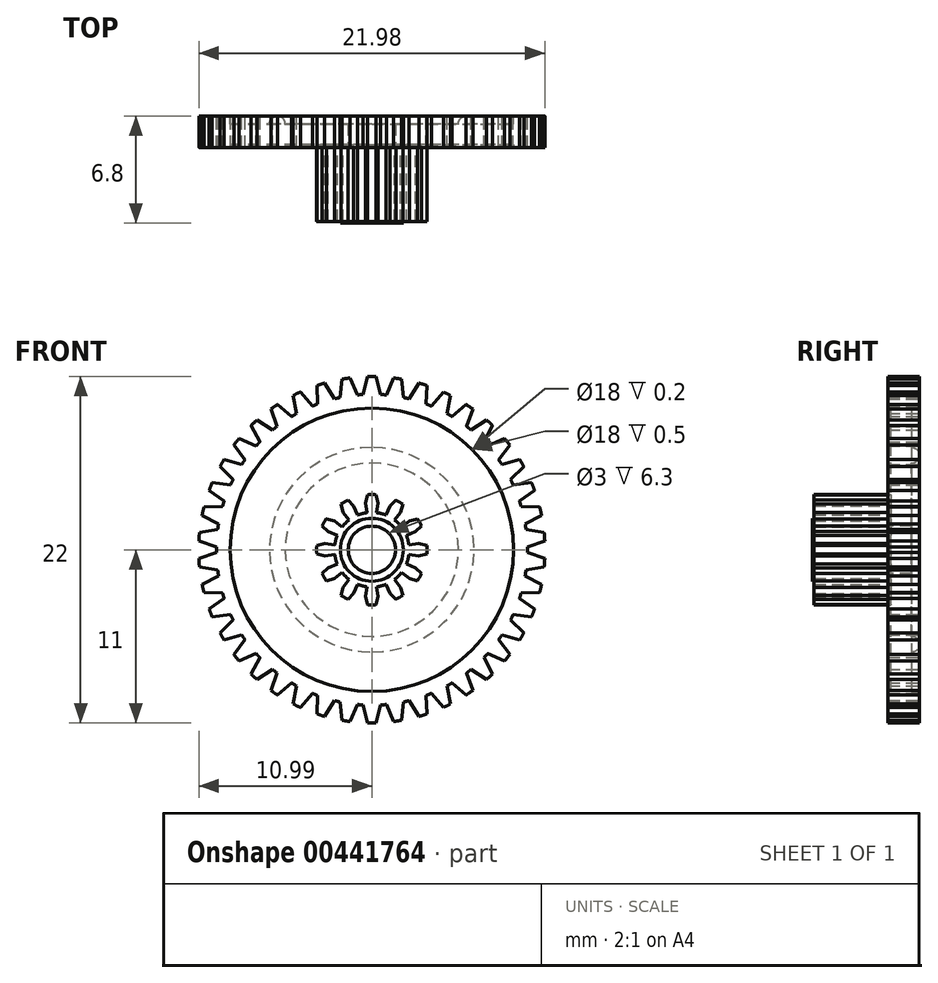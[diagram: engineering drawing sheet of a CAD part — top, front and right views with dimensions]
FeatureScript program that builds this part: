
annotation { "Feature Type Name" : "Feature", "Feature Type Description" : "" }
export const myFeature = defineFeature(function(context is Context, id is Id, definition is map)
    precondition{}
    {
        {
            var Q0;
            Q0=qCreatedBy(makeId("Front.planeOp"),FACE);
            var sketch = newSketch(context, id + "F0", { "sketchPlane" : qUnion([Q0])});
            skCircle(sketch, "E0", {"center": v(0, 0) * mm, "radius": 9.88 * mm});
            skSolve(sketch);
        }
        {
            var Q0;
            Q0 = qSketchRegion(id + "F0", true);
            extrude(context, id + "F1", {"entities" : qUnion([Q0]), "depth" : 2 * mm});
        }
        {
            var Q0;
            Q0=qCreatedBy(makeId("Front.planeOp"),FACE);
            var sketch = newSketch(context, id + "F2", { "sketchPlane" : qUnion([Q0])});
            skArc(sketch, "E1", {"start": v(0, 12) * mm, "mid": v(-0.22, 12) * mm, "end": v(-0.45, 12) * mm});
            skArc(sketch, "E2", {"start": v(0.26, 11) * mm, "mid": v(-0.08, 11) * mm, "end": v(-0.41, 11) * mm});
            skArc(sketch, "E3", {"start": v(0.4, 10.5) * mm, "mid": v(0, 10.5) * mm, "end": v(-0.4, 10.5) * mm});
            skCircle(sketch, "E4", {"center": v(0, 0) * mm, "radius": 9.88 * mm});
            skLineSegment(sketch, "E5", {"start": v(0, 0) * mm, "end": v(0, 15.41) * mm});
            skLineSegment(sketch, "E6", {"start": v(0, 0) * mm, "end": v(-0.5, 13.31) * mm});
            skLineSegment(sketch, "E7", {"start": v(-0.4, 10.5) * mm, "end": v(-0.56, 9.86) * mm});
            skLineSegment(sketch, "E8", {"start": v(0.4, 10.5) * mm, "end": v(0.56, 9.86) * mm});
            skLineSegment(sketch, "E9", {"start": v(-0.4, 10.5) * mm, "end": v(-0.26, 11) * mm});
            skLineSegment(sketch, "E10", {"start": v(-0.26, 11) * mm, "end": v(0, 12) * mm});
            skLineSegment(sketch, "E11", {"start": v(0, 12) * mm, "end": v(0.26, 11) * mm});
            skLineSegment(sketch, "E12", {"start": v(0.26, 11) * mm, "end": v(0.4, 10.5) * mm});
            skLineSegment(sketch, "E13.1.0", {"start": v(-1.95, 10.32) * mm, "end": v(-2.02, 9.67) * mm});
            skLineSegment(sketch, "E13.1.1", {"start": v(-1.95, 10.32) * mm, "end": v(-1.9, 10.84) * mm});
            skLineSegment(sketch, "E13.1.2", {"start": v(-1.38, 10.91) * mm, "end": v(-1.18, 10.43) * mm});
            skLineSegment(sketch, "E13.1.3", {"start": v(-1.18, 10.43) * mm, "end": v(-0.92, 9.83) * mm});
            skArc(sketch, "E13.1.4", {"start": v(-1.38, 10.91) * mm, "mid": v(-1.71, 10.87) * mm, "end": v(-2.05, 10.8) * mm});
            skLineSegment(sketch, "E13.2.0", {"start": v(-3.47, 9.91) * mm, "end": v(-3.44, 9.26) * mm});
            skLineSegment(sketch, "E13.2.1", {"start": v(-3.47, 9.91) * mm, "end": v(-3.5, 10.43) * mm});
            skLineSegment(sketch, "E13.2.2", {"start": v(-3, 10.59) * mm, "end": v(-2.72, 10.14) * mm});
            skLineSegment(sketch, "E13.2.3", {"start": v(-2.72, 10.14) * mm, "end": v(-2.37, 9.59) * mm});
            skArc(sketch, "E13.2.4", {"start": v(-3, 10.59) * mm, "mid": v(-3.31, 10.49) * mm, "end": v(-3.63, 10.38) * mm});
            skLineSegment(sketch, "E13.3.0", {"start": v(-4.9, 9.28) * mm, "end": v(-4.78, 8.64) * mm});
            skLineSegment(sketch, "E13.3.1", {"start": v(-4.9, 9.28) * mm, "end": v(-5, 9.8) * mm});
            skLineSegment(sketch, "E13.3.2", {"start": v(-4.54, 10.02) * mm, "end": v(-4.2, 9.62) * mm});
            skLineSegment(sketch, "E13.3.3", {"start": v(-4.2, 9.62) * mm, "end": v(-3.78, 9.12) * mm});
            skArc(sketch, "E13.3.4", {"start": v(-4.54, 10.02) * mm, "mid": v(-4.84, 9.88) * mm, "end": v(-5.14, 9.73) * mm});
            skLineSegment(sketch, "E13.4.0", {"start": v(-6.24, 8.45) * mm, "end": v(-6.01, 7.83) * mm});
            skLineSegment(sketch, "E13.4.1", {"start": v(-6.24, 8.45) * mm, "end": v(-6.41, 8.94) * mm});
            skLineSegment(sketch, "E13.4.2", {"start": v(-5.98, 9.23) * mm, "end": v(-5.59, 8.9) * mm});
            skLineSegment(sketch, "E13.4.3", {"start": v(-5.59, 8.9) * mm, "end": v(-5.1, 8.46) * mm});
            skArc(sketch, "E13.4.4", {"start": v(-5.98, 9.23) * mm, "mid": v(-6.26, 9.05) * mm, "end": v(-6.53, 8.85) * mm});
            skLineSegment(sketch, "E13.5.0", {"start": v(-7.42, 7.42) * mm, "end": v(-7.11, 6.85) * mm});
            skLineSegment(sketch, "E13.5.1", {"start": v(-7.42, 7.42) * mm, "end": v(-7.67, 7.88) * mm});
            skLineSegment(sketch, "E13.5.2", {"start": v(-7.29, 8.24) * mm, "end": v(-6.85, 7.96) * mm});
            skLineSegment(sketch, "E13.5.3", {"start": v(-6.85, 7.96) * mm, "end": v(-6.3, 7.6) * mm});
            skArc(sketch, "E13.5.4", {"start": v(-7.29, 8.24) * mm, "mid": v(-7.54, 8.01) * mm, "end": v(-7.78, 7.78) * mm});
            skLineSegment(sketch, "E13.6.0", {"start": v(-8.45, 6.24) * mm, "end": v(-8.06, 5.71) * mm});
            skLineSegment(sketch, "E13.6.1", {"start": v(-8.45, 6.24) * mm, "end": v(-8.76, 6.65) * mm});
            skLineSegment(sketch, "E13.6.2", {"start": v(-8.43, 7.06) * mm, "end": v(-7.96, 6.85) * mm});
            skLineSegment(sketch, "E13.6.3", {"start": v(-7.96, 6.85) * mm, "end": v(-7.36, 6.58) * mm});
            skArc(sketch, "E13.6.4", {"start": v(-8.43, 7.06) * mm, "mid": v(-8.65, 6.8) * mm, "end": v(-8.85, 6.53) * mm});
            skLineSegment(sketch, "E13.7.0", {"start": v(-9.28, 4.9) * mm, "end": v(-8.82, 4.45) * mm});
            skLineSegment(sketch, "E13.7.1", {"start": v(-9.28, 4.9) * mm, "end": v(-9.65, 5.27) * mm});
            skLineSegment(sketch, "E13.7.2", {"start": v(-9.4, 5.72) * mm, "end": v(-8.9, 5.59) * mm});
            skLineSegment(sketch, "E13.7.3", {"start": v(-8.9, 5.59) * mm, "end": v(-8.26, 5.41) * mm});
            skArc(sketch, "E13.7.4", {"start": v(-9.4, 5.72) * mm, "mid": v(-9.56, 5.43) * mm, "end": v(-9.73, 5.14) * mm});
            skLineSegment(sketch, "E13.8.0", {"start": v(-9.91, 3.47) * mm, "end": v(-9.38, 3.08) * mm});
            skLineSegment(sketch, "E13.8.1", {"start": v(-9.91, 3.47) * mm, "end": v(-10.33, 3.77) * mm});
            skLineSegment(sketch, "E13.8.2", {"start": v(-10.14, 4.26) * mm, "end": v(-9.62, 4.2) * mm});
            skLineSegment(sketch, "E13.8.3", {"start": v(-9.62, 4.2) * mm, "end": v(-8.97, 4.12) * mm});
            skArc(sketch, "E13.8.4", {"start": v(-10.14, 4.26) * mm, "mid": v(-10.27, 3.95) * mm, "end": v(-10.38, 3.63) * mm});
            skLineSegment(sketch, "E13.9.0", {"start": v(-10.32, 1.95) * mm, "end": v(-9.74, 1.65) * mm});
            skLineSegment(sketch, "E13.9.1", {"start": v(-10.32, 1.95) * mm, "end": v(-10.78, 2.2) * mm});
            skLineSegment(sketch, "E13.9.2", {"start": v(-10.66, 2.7) * mm, "end": v(-10.14, 2.72) * mm});
            skLineSegment(sketch, "E13.9.3", {"start": v(-10.14, 2.72) * mm, "end": v(-9.49, 2.74) * mm});
            skArc(sketch, "E13.9.4", {"start": v(-10.66, 2.7) * mm, "mid": v(-10.74, 2.37) * mm, "end": v(-10.8, 2.05) * mm});
            skLineSegment(sketch, "E13.10.0", {"start": v(-10.5, 0.4) * mm, "end": v(-9.87, 0.18) * mm});
            skLineSegment(sketch, "E13.10.1", {"start": v(-10.5, 0.4) * mm, "end": v(-10.99, 0.56) * mm});
            skLineSegment(sketch, "E13.10.2", {"start": v(-10.95, 1.08) * mm, "end": v(-10.43, 1.18) * mm});
            skLineSegment(sketch, "E13.10.3", {"start": v(-10.43, 1.18) * mm, "end": v(-9.8, 1.3) * mm});
            skArc(sketch, "E13.10.4", {"start": v(-10.95, 1.08) * mm, "mid": v(-10.97, 0.75) * mm, "end": v(-11, 0.41) * mm});
            skLineSegment(sketch, "E13.11.0", {"start": v(-10.43, -1.18) * mm, "end": v(-9.8, -1.3) * mm});
            skLineSegment(sketch, "E13.11.1", {"start": v(-10.43, -1.18) * mm, "end": v(-10.95, -1.08) * mm});
            skLineSegment(sketch, "E13.11.2", {"start": v(-10.99, -0.56) * mm, "end": v(-10.5, -0.4) * mm});
            skLineSegment(sketch, "E13.11.3", {"start": v(-10.5, -0.4) * mm, "end": v(-9.87, -0.18) * mm});
            skArc(sketch, "E13.11.4", {"start": v(-10.99, -0.56) * mm, "mid": v(-10.96, -0.9) * mm, "end": v(-10.93, -1.23) * mm});
            skLineSegment(sketch, "E13.12.0", {"start": v(-10.14, -2.72) * mm, "end": v(-9.49, -2.74) * mm});
            skLineSegment(sketch, "E13.12.1", {"start": v(-10.14, -2.72) * mm, "end": v(-10.66, -2.7) * mm});
            skLineSegment(sketch, "E13.12.2", {"start": v(-10.78, -2.2) * mm, "end": v(-10.32, -1.95) * mm});
            skLineSegment(sketch, "E13.12.3", {"start": v(-10.32, -1.95) * mm, "end": v(-9.74, -1.65) * mm});
            skArc(sketch, "E13.12.4", {"start": v(-10.78, -2.2) * mm, "mid": v(-10.7, -2.52) * mm, "end": v(-10.63, -2.85) * mm});
            skLineSegment(sketch, "E13.13.0", {"start": v(-9.62, -4.2) * mm, "end": v(-8.97, -4.12) * mm});
            skLineSegment(sketch, "E13.13.1", {"start": v(-9.62, -4.2) * mm, "end": v(-10.14, -4.26) * mm});
            skLineSegment(sketch, "E13.13.2", {"start": v(-10.33, -3.77) * mm, "end": v(-9.91, -3.47) * mm});
            skLineSegment(sketch, "E13.13.3", {"start": v(-9.91, -3.47) * mm, "end": v(-9.38, -3.08) * mm});
            skArc(sketch, "E13.13.4", {"start": v(-10.33, -3.77) * mm, "mid": v(-10.21, -4.09) * mm, "end": v(-10.08, -4.4) * mm});
            skLineSegment(sketch, "E13.14.0", {"start": v(-8.9, -5.59) * mm, "end": v(-8.26, -5.41) * mm});
            skLineSegment(sketch, "E13.14.1", {"start": v(-8.9, -5.59) * mm, "end": v(-9.4, -5.72) * mm});
            skLineSegment(sketch, "E13.14.2", {"start": v(-9.65, -5.27) * mm, "end": v(-9.28, -4.9) * mm});
            skLineSegment(sketch, "E13.14.3", {"start": v(-9.28, -4.9) * mm, "end": v(-8.82, -4.45) * mm});
            skArc(sketch, "E13.14.4", {"start": v(-9.65, -5.27) * mm, "mid": v(-9.49, -5.56) * mm, "end": v(-9.31, -5.85) * mm});
            skLineSegment(sketch, "E13.15.0", {"start": v(-7.96, -6.85) * mm, "end": v(-7.36, -6.58) * mm});
            skLineSegment(sketch, "E13.15.1", {"start": v(-7.96, -6.85) * mm, "end": v(-8.43, -7.06) * mm});
            skLineSegment(sketch, "E13.15.2", {"start": v(-8.76, -6.65) * mm, "end": v(-8.45, -6.24) * mm});
            skLineSegment(sketch, "E13.15.3", {"start": v(-8.45, -6.24) * mm, "end": v(-8.06, -5.71) * mm});
            skArc(sketch, "E13.15.4", {"start": v(-8.76, -6.65) * mm, "mid": v(-8.55, -6.92) * mm, "end": v(-8.34, -7.18) * mm});
            skLineSegment(sketch, "E13.16.0", {"start": v(-6.85, -7.96) * mm, "end": v(-6.3, -7.6) * mm});
            skLineSegment(sketch, "E13.16.1", {"start": v(-6.85, -7.96) * mm, "end": v(-7.29, -8.24) * mm});
            skLineSegment(sketch, "E13.16.2", {"start": v(-7.67, -7.88) * mm, "end": v(-7.42, -7.42) * mm});
            skLineSegment(sketch, "E13.16.3", {"start": v(-7.42, -7.42) * mm, "end": v(-7.11, -6.85) * mm});
            skArc(sketch, "E13.16.4", {"start": v(-7.67, -7.88) * mm, "mid": v(-7.43, -8.11) * mm, "end": v(-7.18, -8.34) * mm});
            skLineSegment(sketch, "E13.17.0", {"start": v(-5.59, -8.9) * mm, "end": v(-5.1, -8.46) * mm});
            skLineSegment(sketch, "E13.17.1", {"start": v(-5.59, -8.9) * mm, "end": v(-5.98, -9.23) * mm});
            skLineSegment(sketch, "E13.17.2", {"start": v(-6.41, -8.94) * mm, "end": v(-6.24, -8.45) * mm});
            skLineSegment(sketch, "E13.17.3", {"start": v(-6.24, -8.45) * mm, "end": v(-6.01, -7.83) * mm});
            skArc(sketch, "E13.17.4", {"start": v(-6.41, -8.94) * mm, "mid": v(-6.13, -9.13) * mm, "end": v(-5.85, -9.31) * mm});
            skLineSegment(sketch, "E13.18.0", {"start": v(-4.2, -9.62) * mm, "end": v(-3.78, -9.12) * mm});
            skLineSegment(sketch, "E13.18.1", {"start": v(-4.2, -9.62) * mm, "end": v(-4.54, -10.02) * mm});
            skLineSegment(sketch, "E13.18.2", {"start": v(-5, -9.8) * mm, "end": v(-4.9, -9.28) * mm});
            skLineSegment(sketch, "E13.18.3", {"start": v(-4.9, -9.28) * mm, "end": v(-4.78, -8.64) * mm});
            skArc(sketch, "E13.18.4", {"start": v(-5, -9.8) * mm, "mid": v(-4.7, -9.94) * mm, "end": v(-4.4, -10.08) * mm});
            skLineSegment(sketch, "E13.19.0", {"start": v(-2.72, -10.14) * mm, "end": v(-2.37, -9.59) * mm});
            skLineSegment(sketch, "E13.19.1", {"start": v(-2.72, -10.14) * mm, "end": v(-3, -10.59) * mm});
            skLineSegment(sketch, "E13.19.2", {"start": v(-3.5, -10.43) * mm, "end": v(-3.47, -9.91) * mm});
            skLineSegment(sketch, "E13.19.3", {"start": v(-3.47, -9.91) * mm, "end": v(-3.44, -9.26) * mm});
            skArc(sketch, "E13.19.4", {"start": v(-3.5, -10.43) * mm, "mid": v(-3.17, -10.53) * mm, "end": v(-2.85, -10.63) * mm});
            skLineSegment(sketch, "E13.20.0", {"start": v(-1.18, -10.43) * mm, "end": v(-0.92, -9.83) * mm});
            skLineSegment(sketch, "E13.20.1", {"start": v(-1.18, -10.43) * mm, "end": v(-1.38, -10.91) * mm});
            skLineSegment(sketch, "E13.20.2", {"start": v(-1.9, -10.84) * mm, "end": v(-1.95, -10.32) * mm});
            skLineSegment(sketch, "E13.20.3", {"start": v(-1.95, -10.32) * mm, "end": v(-2.02, -9.67) * mm});
            skArc(sketch, "E13.20.4", {"start": v(-1.9, -10.84) * mm, "mid": v(-1.57, -10.89) * mm, "end": v(-1.23, -10.93) * mm});
            skLineSegment(sketch, "E13.21.0", {"start": v(0.4, -10.5) * mm, "end": v(0.56, -9.86) * mm});
            skLineSegment(sketch, "E13.21.1", {"start": v(0.4, -10.5) * mm, "end": v(0.26, -11) * mm});
            skLineSegment(sketch, "E13.21.2", {"start": v(-0.26, -11) * mm, "end": v(-0.4, -10.5) * mm});
            skLineSegment(sketch, "E13.21.3", {"start": v(-0.4, -10.5) * mm, "end": v(-0.56, -9.86) * mm});
            skArc(sketch, "E13.21.4", {"start": v(-0.26, -11) * mm, "mid": v(0.08, -11) * mm, "end": v(0.41, -11) * mm});
            skLineSegment(sketch, "E13.22.0", {"start": v(1.95, -10.32) * mm, "end": v(2.02, -9.67) * mm});
            skLineSegment(sketch, "E13.22.1", {"start": v(1.95, -10.32) * mm, "end": v(1.9, -10.84) * mm});
            skLineSegment(sketch, "E13.22.2", {"start": v(1.38, -10.91) * mm, "end": v(1.18, -10.43) * mm});
            skLineSegment(sketch, "E13.22.3", {"start": v(1.18, -10.43) * mm, "end": v(0.92, -9.83) * mm});
            skArc(sketch, "E13.22.4", {"start": v(1.38, -10.91) * mm, "mid": v(1.71, -10.87) * mm, "end": v(2.05, -10.8) * mm});
            skLineSegment(sketch, "E13.23.0", {"start": v(3.47, -9.91) * mm, "end": v(3.44, -9.26) * mm});
            skLineSegment(sketch, "E13.23.1", {"start": v(3.47, -9.91) * mm, "end": v(3.5, -10.43) * mm});
            skLineSegment(sketch, "E13.23.2", {"start": v(3, -10.59) * mm, "end": v(2.72, -10.14) * mm});
            skLineSegment(sketch, "E13.23.3", {"start": v(2.72, -10.14) * mm, "end": v(2.37, -9.59) * mm});
            skArc(sketch, "E13.23.4", {"start": v(3, -10.59) * mm, "mid": v(3.31, -10.49) * mm, "end": v(3.63, -10.38) * mm});
            skLineSegment(sketch, "E13.24.0", {"start": v(4.9, -9.28) * mm, "end": v(4.78, -8.64) * mm});
            skLineSegment(sketch, "E13.24.1", {"start": v(4.9, -9.28) * mm, "end": v(5, -9.8) * mm});
            skLineSegment(sketch, "E13.24.2", {"start": v(4.54, -10.02) * mm, "end": v(4.2, -9.62) * mm});
            skLineSegment(sketch, "E13.24.3", {"start": v(4.2, -9.62) * mm, "end": v(3.78, -9.12) * mm});
            skArc(sketch, "E13.24.4", {"start": v(4.54, -10.02) * mm, "mid": v(4.84, -9.88) * mm, "end": v(5.14, -9.73) * mm});
            skLineSegment(sketch, "E13.25.0", {"start": v(6.24, -8.45) * mm, "end": v(6.01, -7.83) * mm});
            skLineSegment(sketch, "E13.25.1", {"start": v(6.24, -8.45) * mm, "end": v(6.41, -8.94) * mm});
            skLineSegment(sketch, "E13.25.2", {"start": v(5.98, -9.23) * mm, "end": v(5.59, -8.9) * mm});
            skLineSegment(sketch, "E13.25.3", {"start": v(5.59, -8.9) * mm, "end": v(5.1, -8.46) * mm});
            skArc(sketch, "E13.25.4", {"start": v(5.98, -9.23) * mm, "mid": v(6.26, -9.05) * mm, "end": v(6.53, -8.85) * mm});
            skLineSegment(sketch, "E13.26.0", {"start": v(7.42, -7.42) * mm, "end": v(7.11, -6.85) * mm});
            skLineSegment(sketch, "E13.26.1", {"start": v(7.42, -7.42) * mm, "end": v(7.67, -7.88) * mm});
            skLineSegment(sketch, "E13.26.2", {"start": v(7.29, -8.24) * mm, "end": v(6.85, -7.96) * mm});
            skLineSegment(sketch, "E13.26.3", {"start": v(6.85, -7.96) * mm, "end": v(6.3, -7.6) * mm});
            skArc(sketch, "E13.26.4", {"start": v(7.29, -8.24) * mm, "mid": v(7.54, -8.01) * mm, "end": v(7.78, -7.78) * mm});
            skLineSegment(sketch, "E13.27.0", {"start": v(8.45, -6.24) * mm, "end": v(8.06, -5.71) * mm});
            skLineSegment(sketch, "E13.27.1", {"start": v(8.45, -6.24) * mm, "end": v(8.76, -6.65) * mm});
            skLineSegment(sketch, "E13.27.2", {"start": v(8.43, -7.06) * mm, "end": v(7.96, -6.85) * mm});
            skLineSegment(sketch, "E13.27.3", {"start": v(7.96, -6.85) * mm, "end": v(7.36, -6.58) * mm});
            skArc(sketch, "E13.27.4", {"start": v(8.43, -7.06) * mm, "mid": v(8.65, -6.8) * mm, "end": v(8.85, -6.53) * mm});
            skLineSegment(sketch, "E13.28.0", {"start": v(9.28, -4.9) * mm, "end": v(8.82, -4.45) * mm});
            skLineSegment(sketch, "E13.28.1", {"start": v(9.28, -4.9) * mm, "end": v(9.65, -5.27) * mm});
            skLineSegment(sketch, "E13.28.2", {"start": v(9.4, -5.72) * mm, "end": v(8.9, -5.59) * mm});
            skLineSegment(sketch, "E13.28.3", {"start": v(8.9, -5.59) * mm, "end": v(8.26, -5.41) * mm});
            skArc(sketch, "E13.28.4", {"start": v(9.4, -5.72) * mm, "mid": v(9.56, -5.43) * mm, "end": v(9.73, -5.14) * mm});
            skLineSegment(sketch, "E13.29.0", {"start": v(9.91, -3.47) * mm, "end": v(9.38, -3.08) * mm});
            skLineSegment(sketch, "E13.29.1", {"start": v(9.91, -3.47) * mm, "end": v(10.33, -3.77) * mm});
            skLineSegment(sketch, "E13.29.2", {"start": v(10.14, -4.26) * mm, "end": v(9.62, -4.2) * mm});
            skLineSegment(sketch, "E13.29.3", {"start": v(9.62, -4.2) * mm, "end": v(8.97, -4.12) * mm});
            skArc(sketch, "E13.29.4", {"start": v(10.14, -4.26) * mm, "mid": v(10.27, -3.95) * mm, "end": v(10.38, -3.63) * mm});
            skLineSegment(sketch, "E13.30.0", {"start": v(10.32, -1.95) * mm, "end": v(9.74, -1.65) * mm});
            skLineSegment(sketch, "E13.30.1", {"start": v(10.32, -1.95) * mm, "end": v(10.78, -2.2) * mm});
            skLineSegment(sketch, "E13.30.2", {"start": v(10.66, -2.7) * mm, "end": v(10.14, -2.72) * mm});
            skLineSegment(sketch, "E13.30.3", {"start": v(10.14, -2.72) * mm, "end": v(9.49, -2.74) * mm});
            skArc(sketch, "E13.30.4", {"start": v(10.66, -2.7) * mm, "mid": v(10.74, -2.37) * mm, "end": v(10.8, -2.05) * mm});
            skLineSegment(sketch, "E13.31.0", {"start": v(10.5, -0.4) * mm, "end": v(9.87, -0.18) * mm});
            skLineSegment(sketch, "E13.31.1", {"start": v(10.5, -0.4) * mm, "end": v(10.99, -0.56) * mm});
            skLineSegment(sketch, "E13.31.2", {"start": v(10.95, -1.08) * mm, "end": v(10.43, -1.18) * mm});
            skLineSegment(sketch, "E13.31.3", {"start": v(10.43, -1.18) * mm, "end": v(9.8, -1.3) * mm});
            skArc(sketch, "E13.31.4", {"start": v(10.95, -1.08) * mm, "mid": v(10.97, -0.75) * mm, "end": v(11, -0.41) * mm});
            skLineSegment(sketch, "E13.32.0", {"start": v(10.43, 1.18) * mm, "end": v(9.8, 1.3) * mm});
            skLineSegment(sketch, "E13.32.1", {"start": v(10.43, 1.18) * mm, "end": v(10.95, 1.08) * mm});
            skLineSegment(sketch, "E13.32.2", {"start": v(10.99, 0.56) * mm, "end": v(10.5, 0.4) * mm});
            skLineSegment(sketch, "E13.32.3", {"start": v(10.5, 0.4) * mm, "end": v(9.87, 0.18) * mm});
            skArc(sketch, "E13.32.4", {"start": v(10.99, 0.56) * mm, "mid": v(10.96, 0.9) * mm, "end": v(10.93, 1.23) * mm});
            skLineSegment(sketch, "E13.33.0", {"start": v(10.14, 2.72) * mm, "end": v(9.49, 2.74) * mm});
            skLineSegment(sketch, "E13.33.1", {"start": v(10.14, 2.72) * mm, "end": v(10.66, 2.7) * mm});
            skLineSegment(sketch, "E13.33.2", {"start": v(10.78, 2.2) * mm, "end": v(10.32, 1.95) * mm});
            skLineSegment(sketch, "E13.33.3", {"start": v(10.32, 1.95) * mm, "end": v(9.74, 1.65) * mm});
            skArc(sketch, "E13.33.4", {"start": v(10.78, 2.2) * mm, "mid": v(10.7, 2.52) * mm, "end": v(10.63, 2.85) * mm});
            skLineSegment(sketch, "E13.34.0", {"start": v(9.62, 4.2) * mm, "end": v(8.97, 4.12) * mm});
            skLineSegment(sketch, "E13.34.1", {"start": v(9.62, 4.2) * mm, "end": v(10.14, 4.26) * mm});
            skLineSegment(sketch, "E13.34.2", {"start": v(10.33, 3.77) * mm, "end": v(9.91, 3.47) * mm});
            skLineSegment(sketch, "E13.34.3", {"start": v(9.91, 3.47) * mm, "end": v(9.38, 3.08) * mm});
            skArc(sketch, "E13.34.4", {"start": v(10.33, 3.77) * mm, "mid": v(10.21, 4.09) * mm, "end": v(10.08, 4.4) * mm});
            skLineSegment(sketch, "E13.35.0", {"start": v(8.9, 5.59) * mm, "end": v(8.26, 5.41) * mm});
            skLineSegment(sketch, "E13.35.1", {"start": v(8.9, 5.59) * mm, "end": v(9.4, 5.72) * mm});
            skLineSegment(sketch, "E13.35.2", {"start": v(9.65, 5.27) * mm, "end": v(9.28, 4.9) * mm});
            skLineSegment(sketch, "E13.35.3", {"start": v(9.28, 4.9) * mm, "end": v(8.82, 4.45) * mm});
            skArc(sketch, "E13.35.4", {"start": v(9.65, 5.27) * mm, "mid": v(9.49, 5.56) * mm, "end": v(9.31, 5.85) * mm});
            skLineSegment(sketch, "E13.36.0", {"start": v(7.96, 6.85) * mm, "end": v(7.36, 6.58) * mm});
            skLineSegment(sketch, "E13.36.1", {"start": v(7.96, 6.85) * mm, "end": v(8.43, 7.06) * mm});
            skLineSegment(sketch, "E13.36.2", {"start": v(8.76, 6.65) * mm, "end": v(8.45, 6.24) * mm});
            skLineSegment(sketch, "E13.36.3", {"start": v(8.45, 6.24) * mm, "end": v(8.06, 5.71) * mm});
            skArc(sketch, "E13.36.4", {"start": v(8.76, 6.65) * mm, "mid": v(8.55, 6.92) * mm, "end": v(8.34, 7.18) * mm});
            skLineSegment(sketch, "E13.37.0", {"start": v(6.85, 7.96) * mm, "end": v(6.3, 7.6) * mm});
            skLineSegment(sketch, "E13.37.1", {"start": v(6.85, 7.96) * mm, "end": v(7.29, 8.24) * mm});
            skLineSegment(sketch, "E13.37.2", {"start": v(7.67, 7.88) * mm, "end": v(7.42, 7.42) * mm});
            skLineSegment(sketch, "E13.37.3", {"start": v(7.42, 7.42) * mm, "end": v(7.11, 6.85) * mm});
            skArc(sketch, "E13.37.4", {"start": v(7.67, 7.88) * mm, "mid": v(7.43, 8.11) * mm, "end": v(7.18, 8.34) * mm});
            skLineSegment(sketch, "E13.38.0", {"start": v(5.59, 8.9) * mm, "end": v(5.1, 8.46) * mm});
            skLineSegment(sketch, "E13.38.1", {"start": v(5.59, 8.9) * mm, "end": v(5.98, 9.23) * mm});
            skLineSegment(sketch, "E13.38.2", {"start": v(6.41, 8.94) * mm, "end": v(6.24, 8.45) * mm});
            skLineSegment(sketch, "E13.38.3", {"start": v(6.24, 8.45) * mm, "end": v(6.01, 7.83) * mm});
            skArc(sketch, "E13.38.4", {"start": v(6.41, 8.94) * mm, "mid": v(6.13, 9.13) * mm, "end": v(5.85, 9.31) * mm});
            skLineSegment(sketch, "E13.39.0", {"start": v(4.2, 9.62) * mm, "end": v(3.78, 9.12) * mm});
            skLineSegment(sketch, "E13.39.1", {"start": v(4.2, 9.62) * mm, "end": v(4.54, 10.02) * mm});
            skLineSegment(sketch, "E13.39.2", {"start": v(5, 9.8) * mm, "end": v(4.9, 9.28) * mm});
            skLineSegment(sketch, "E13.39.3", {"start": v(4.9, 9.28) * mm, "end": v(4.78, 8.64) * mm});
            skArc(sketch, "E13.39.4", {"start": v(5, 9.8) * mm, "mid": v(4.7, 9.94) * mm, "end": v(4.4, 10.08) * mm});
            skLineSegment(sketch, "E13.40.0", {"start": v(2.72, 10.14) * mm, "end": v(2.37, 9.59) * mm});
            skLineSegment(sketch, "E13.40.1", {"start": v(2.72, 10.14) * mm, "end": v(3, 10.59) * mm});
            skLineSegment(sketch, "E13.40.2", {"start": v(3.5, 10.43) * mm, "end": v(3.47, 9.91) * mm});
            skLineSegment(sketch, "E13.40.3", {"start": v(3.47, 9.91) * mm, "end": v(3.44, 9.26) * mm});
            skArc(sketch, "E13.40.4", {"start": v(3.5, 10.43) * mm, "mid": v(3.17, 10.53) * mm, "end": v(2.85, 10.63) * mm});
            skLineSegment(sketch, "E13.41.0", {"start": v(1.18, 10.43) * mm, "end": v(0.92, 9.83) * mm});
            skLineSegment(sketch, "E13.41.1", {"start": v(1.18, 10.43) * mm, "end": v(1.38, 10.91) * mm});
            skLineSegment(sketch, "E13.41.2", {"start": v(1.9, 10.84) * mm, "end": v(1.95, 10.32) * mm});
            skLineSegment(sketch, "E13.41.3", {"start": v(1.95, 10.32) * mm, "end": v(2.02, 9.67) * mm});
            skArc(sketch, "E13.41.4", {"start": v(1.9, 10.84) * mm, "mid": v(1.57, 10.89) * mm, "end": v(1.23, 10.93) * mm});
            skSolve(sketch);
        }
        {
            var Q0;
            {var subQ2=sQuery(id+"F2.wireOp",EDGE,"E13.32.0");Q0=makeQuery(id+"F2.imprint","IMPRINT",FACE,{"disambiguationData":[TD([[makeQuery(id+"F2.imprint","IMPRINT",EDGE,{"derivedFrom":subQ2}),1.0]])]});}
            var Q1;
            {var subQ1=sQuery(id+"F2.wireOp",EDGE,"E13.33.0");Q1=makeQuery(id+"F2.imprint","IMPRINT",FACE,{"disambiguationData":[TD([[makeQuery(id+"F2.imprint","IMPRINT",EDGE,{"derivedFrom":subQ1}),1.0]])]});}
            var Q2;
            {var subQ2=sQuery(id+"F2.wireOp",EDGE,"E13.34.0");Q2=makeQuery(id+"F2.imprint","IMPRINT",FACE,{"disambiguationData":[TD([[makeQuery(id+"F2.imprint","IMPRINT",EDGE,{"derivedFrom":subQ2}),1.0]])]});}
            var Q3;
            {var subQ1=sQuery(id+"F2.wireOp",EDGE,"E13.35.0");Q3=makeQuery(id+"F2.imprint","IMPRINT",FACE,{"disambiguationData":[TD([[makeQuery(id+"F2.imprint","IMPRINT",EDGE,{"derivedFrom":subQ1}),1.0]])]});}
            var Q4;
            {var subQ2=sQuery(id+"F2.wireOp",EDGE,"E13.36.0");Q4=makeQuery(id+"F2.imprint","IMPRINT",FACE,{"disambiguationData":[TD([[makeQuery(id+"F2.imprint","IMPRINT",EDGE,{"derivedFrom":subQ2}),1.0]])]});}
            var Q5;
            {var subQ2=sQuery(id+"F2.wireOp",EDGE,"E13.37.0");Q5=makeQuery(id+"F2.imprint","IMPRINT",FACE,{"disambiguationData":[TD([[makeQuery(id+"F2.imprint","IMPRINT",EDGE,{"derivedFrom":subQ2}),1.0]])]});}
            var Q6;
            {var subQ1=sQuery(id+"F2.wireOp",EDGE,"E13.38.0");Q6=makeQuery(id+"F2.imprint","IMPRINT",FACE,{"disambiguationData":[TD([[makeQuery(id+"F2.imprint","IMPRINT",EDGE,{"derivedFrom":subQ1}),1.0]])]});}
            var Q7;
            {var subQ2=sQuery(id+"F2.wireOp",EDGE,"E13.39.0");Q7=makeQuery(id+"F2.imprint","IMPRINT",FACE,{"disambiguationData":[TD([[makeQuery(id+"F2.imprint","IMPRINT",EDGE,{"derivedFrom":subQ2}),1.0]])]});}
            var Q8;
            {var subQ1=sQuery(id+"F2.wireOp",EDGE,"E13.40.0");Q8=makeQuery(id+"F2.imprint","IMPRINT",FACE,{"disambiguationData":[TD([[makeQuery(id+"F2.imprint","IMPRINT",EDGE,{"derivedFrom":subQ1}),1.0]])]});}
            var Q9;
            {var subQ2=sQuery(id+"F2.wireOp",EDGE,"E13.41.0");Q9=makeQuery(id+"F2.imprint","IMPRINT",FACE,{"disambiguationData":[TD([[makeQuery(id+"F2.imprint","IMPRINT",EDGE,{"derivedFrom":subQ2}),1.0]])]});}
            var Q10;
            {var subQ2=sQuery(id+"F2.wireOp",EDGE,"E13.1.0");Q10=makeQuery(id+"F2.imprint","IMPRINT",FACE,{"disambiguationData":[TD([[makeQuery(id+"F2.imprint","IMPRINT",EDGE,{"derivedFrom":subQ2}),1.0]])]});}
            var Q11;
            {var subQ1=sQuery(id+"F2.wireOp",EDGE,"E13.2.0");Q11=makeQuery(id+"F2.imprint","IMPRINT",FACE,{"disambiguationData":[TD([[makeQuery(id+"F2.imprint","IMPRINT",EDGE,{"derivedFrom":subQ1}),1.0]])]});}
            var Q12;
            {var subQ2=sQuery(id+"F2.wireOp",EDGE,"E13.3.0");Q12=makeQuery(id+"F2.imprint","IMPRINT",FACE,{"disambiguationData":[TD([[makeQuery(id+"F2.imprint","IMPRINT",EDGE,{"derivedFrom":subQ2}),1.0]])]});}
            var Q13;
            {var subQ2=sQuery(id+"F2.wireOp",EDGE,"E13.4.0");Q13=makeQuery(id+"F2.imprint","IMPRINT",FACE,{"disambiguationData":[TD([[makeQuery(id+"F2.imprint","IMPRINT",EDGE,{"derivedFrom":subQ2}),1.0]])]});}
            var Q14;
            {var subQ1=sQuery(id+"F2.wireOp",EDGE,"E13.5.0");Q14=makeQuery(id+"F2.imprint","IMPRINT",FACE,{"disambiguationData":[TD([[makeQuery(id+"F2.imprint","IMPRINT",EDGE,{"derivedFrom":subQ1}),1.0]])]});}
            var Q15;
            {var subQ2=sQuery(id+"F2.wireOp",EDGE,"E13.6.0");Q15=makeQuery(id+"F2.imprint","IMPRINT",FACE,{"disambiguationData":[TD([[makeQuery(id+"F2.imprint","IMPRINT",EDGE,{"derivedFrom":subQ2}),1.0]])]});}
            var Q16;
            {var subQ1=sQuery(id+"F2.wireOp",EDGE,"E13.7.0");Q16=makeQuery(id+"F2.imprint","IMPRINT",FACE,{"disambiguationData":[TD([[makeQuery(id+"F2.imprint","IMPRINT",EDGE,{"derivedFrom":subQ1}),1.0]])]});}
            var Q17;
            {var subQ1=sQuery(id+"F2.wireOp",EDGE,"E13.8.0");Q17=makeQuery(id+"F2.imprint","IMPRINT",FACE,{"disambiguationData":[TD([[makeQuery(id+"F2.imprint","IMPRINT",EDGE,{"derivedFrom":subQ1}),1.0]])]});}
            var Q18;
            {var subQ2=sQuery(id+"F2.wireOp",EDGE,"E13.9.0");Q18=makeQuery(id+"F2.imprint","IMPRINT",FACE,{"disambiguationData":[TD([[makeQuery(id+"F2.imprint","IMPRINT",EDGE,{"derivedFrom":subQ2}),1.0]])]});}
            var Q19;
            {var subQ1=sQuery(id+"F2.wireOp",EDGE,"E13.10.0");Q19=makeQuery(id+"F2.imprint","IMPRINT",FACE,{"disambiguationData":[TD([[makeQuery(id+"F2.imprint","IMPRINT",EDGE,{"derivedFrom":subQ1}),1.0]])]});}
            var Q20;
            {var subQ2=sQuery(id+"F2.wireOp",EDGE,"E13.11.0");Q20=makeQuery(id+"F2.imprint","IMPRINT",FACE,{"disambiguationData":[TD([[makeQuery(id+"F2.imprint","IMPRINT",EDGE,{"derivedFrom":subQ2}),1.0]])]});}
            var Q21;
            {var subQ1=sQuery(id+"F2.wireOp",EDGE,"E13.12.0");Q21=makeQuery(id+"F2.imprint","IMPRINT",FACE,{"disambiguationData":[TD([[makeQuery(id+"F2.imprint","IMPRINT",EDGE,{"derivedFrom":subQ1}),1.0]])]});}
            var Q22;
            {var subQ2=sQuery(id+"F2.wireOp",EDGE,"E13.13.0");Q22=makeQuery(id+"F2.imprint","IMPRINT",FACE,{"disambiguationData":[TD([[makeQuery(id+"F2.imprint","IMPRINT",EDGE,{"derivedFrom":subQ2}),1.0]])]});}
            var Q23;
            {var subQ2=sQuery(id+"F2.wireOp",EDGE,"E13.14.0");Q23=makeQuery(id+"F2.imprint","IMPRINT",FACE,{"disambiguationData":[TD([[makeQuery(id+"F2.imprint","IMPRINT",EDGE,{"derivedFrom":subQ2}),1.0]])]});}
            var Q24;
            {var subQ1=sQuery(id+"F2.wireOp",EDGE,"E13.15.0");Q24=makeQuery(id+"F2.imprint","IMPRINT",FACE,{"disambiguationData":[TD([[makeQuery(id+"F2.imprint","IMPRINT",EDGE,{"derivedFrom":subQ1}),1.0]])]});}
            var Q25;
            {var subQ2=sQuery(id+"F2.wireOp",EDGE,"E13.16.0");Q25=makeQuery(id+"F2.imprint","IMPRINT",FACE,{"disambiguationData":[TD([[makeQuery(id+"F2.imprint","IMPRINT",EDGE,{"derivedFrom":subQ2}),1.0]])]});}
            var Q26;
            {var subQ1=sQuery(id+"F2.wireOp",EDGE,"E13.17.0");Q26=makeQuery(id+"F2.imprint","IMPRINT",FACE,{"disambiguationData":[TD([[makeQuery(id+"F2.imprint","IMPRINT",EDGE,{"derivedFrom":subQ1}),1.0]])]});}
            var Q27;
            {var subQ2=sQuery(id+"F2.wireOp",EDGE,"E13.18.0");Q27=makeQuery(id+"F2.imprint","IMPRINT",FACE,{"disambiguationData":[TD([[makeQuery(id+"F2.imprint","IMPRINT",EDGE,{"derivedFrom":subQ2}),1.0]])]});}
            var Q28;
            {var subQ1=sQuery(id+"F2.wireOp",EDGE,"E13.19.0");Q28=makeQuery(id+"F2.imprint","IMPRINT",FACE,{"disambiguationData":[TD([[makeQuery(id+"F2.imprint","IMPRINT",EDGE,{"derivedFrom":subQ1}),1.0]])]});}
            var Q29;
            {var subQ1=sQuery(id+"F2.wireOp",EDGE,"E13.20.0");Q29=makeQuery(id+"F2.imprint","IMPRINT",FACE,{"disambiguationData":[TD([[makeQuery(id+"F2.imprint","IMPRINT",EDGE,{"derivedFrom":subQ1}),1.0]])]});}
            var Q30;
            {var subQ2=sQuery(id+"F2.wireOp",EDGE,"E13.21.0");Q30=makeQuery(id+"F2.imprint","IMPRINT",FACE,{"disambiguationData":[TD([[makeQuery(id+"F2.imprint","IMPRINT",EDGE,{"derivedFrom":subQ2}),1.0]])]});}
            var Q31;
            {var subQ1=sQuery(id+"F2.wireOp",EDGE,"E13.22.0");Q31=makeQuery(id+"F2.imprint","IMPRINT",FACE,{"disambiguationData":[TD([[makeQuery(id+"F2.imprint","IMPRINT",EDGE,{"derivedFrom":subQ1}),1.0]])]});}
            var Q32;
            {var subQ2=sQuery(id+"F2.wireOp",EDGE,"E13.23.0");Q32=makeQuery(id+"F2.imprint","IMPRINT",FACE,{"disambiguationData":[TD([[makeQuery(id+"F2.imprint","IMPRINT",EDGE,{"derivedFrom":subQ2}),1.0]])]});}
            var Q33;
            {var subQ2=sQuery(id+"F2.wireOp",EDGE,"E13.24.0");Q33=makeQuery(id+"F2.imprint","IMPRINT",FACE,{"disambiguationData":[TD([[makeQuery(id+"F2.imprint","IMPRINT",EDGE,{"derivedFrom":subQ2}),1.0]])]});}
            var Q34;
            {var subQ1=sQuery(id+"F2.wireOp",EDGE,"E13.25.0");Q34=makeQuery(id+"F2.imprint","IMPRINT",FACE,{"disambiguationData":[TD([[makeQuery(id+"F2.imprint","IMPRINT",EDGE,{"derivedFrom":subQ1}),1.0]])]});}
            var Q35;
            {var subQ2=sQuery(id+"F2.wireOp",EDGE,"E13.26.0");Q35=makeQuery(id+"F2.imprint","IMPRINT",FACE,{"disambiguationData":[TD([[makeQuery(id+"F2.imprint","IMPRINT",EDGE,{"derivedFrom":subQ2}),1.0]])]});}
            var Q36;
            {var subQ1=sQuery(id+"F2.wireOp",EDGE,"E13.27.0");Q36=makeQuery(id+"F2.imprint","IMPRINT",FACE,{"disambiguationData":[TD([[makeQuery(id+"F2.imprint","IMPRINT",EDGE,{"derivedFrom":subQ1}),1.0]])]});}
            var Q37;
            {var subQ2=sQuery(id+"F2.wireOp",EDGE,"E13.28.0");Q37=makeQuery(id+"F2.imprint","IMPRINT",FACE,{"disambiguationData":[TD([[makeQuery(id+"F2.imprint","IMPRINT",EDGE,{"derivedFrom":subQ2}),1.0]])]});}
            var Q38;
            {var subQ2=sQuery(id+"F2.wireOp",EDGE,"E13.29.0");Q38=makeQuery(id+"F2.imprint","IMPRINT",FACE,{"disambiguationData":[TD([[makeQuery(id+"F2.imprint","IMPRINT",EDGE,{"derivedFrom":subQ2}),1.0]])]});}
            var Q39;
            {var subQ1=sQuery(id+"F2.wireOp",EDGE,"E13.30.0");Q39=makeQuery(id+"F2.imprint","IMPRINT",FACE,{"disambiguationData":[TD([[makeQuery(id+"F2.imprint","IMPRINT",EDGE,{"derivedFrom":subQ1}),1.0]])]});}
            var Q40;
            {var subQ2=sQuery(id+"F2.wireOp",EDGE,"E13.31.0");Q40=makeQuery(id+"F2.imprint","IMPRINT",FACE,{"disambiguationData":[TD([[makeQuery(id+"F2.imprint","IMPRINT",EDGE,{"derivedFrom":subQ2}),1.0]])]});}
            var Q41;
            {var subQ0=sQuery(id+"F2.wireOp",EDGE,"E7");Q41=makeQuery(id+"F2.imprint","IMPRINT",FACE,{"disambiguationData":[TD([[makeQuery(id+"F2.imprint","IMPRINT",EDGE,{"derivedFrom":subQ0}),1.0]])]});}
            var Q42;
            {var subQ0=sQuery(id+"F2.wireOp",EDGE,"E12");Q42=makeQuery(id+"F2.imprint","IMPRINT",FACE,{"disambiguationData":[TD([[makeQuery(id+"F2.imprint","IMPRINT",EDGE,{"derivedFrom":subQ0}),-1.0]])]});}
            var Q43;
            {var subQ0=sQuery(id+"F2.wireOp",EDGE,"E8");Q43=makeQuery(id+"F2.imprint","IMPRINT",FACE,{"disambiguationData":[TD([[makeQuery(id+"F2.imprint","IMPRINT",EDGE,{"derivedFrom":subQ0}),-1.0]])]});}
            var Q44;
            {var subQ0=sQuery(id+"F2.wireOp",EDGE,"E9");Q44=makeQuery(id+"F2.imprint","IMPRINT",FACE,{"disambiguationData":[TD([[makeQuery(id+"F2.imprint","IMPRINT",EDGE,{"derivedFrom":subQ0}),-1.0]])]});}
            var Q45;
            {var subQ3=sQuery(id+"F2.wireOp",EDGE,"E5");var subQ5=sQuery(id+"F2.wireOp",EDGE,"E4");var subQ6=makeQuery(id+"F2.imprint","INTERSECT",VERTEX,{"derivedFrom":[subQ5,subQ3]});Q45=makeQuery(id+"F2.imprint","IMPRINT",FACE,{"disambiguationData":[TD([[makeQuery(id+"F2.imprint","IMPRINT",EDGE,{"disambiguationData":[TD([[subQ6,-1.0]])],"derivedFrom":subQ5}),-1.0]])]});}
            extrude(context, id + "F3", {"entities" : qUnion([Q0, Q1, Q2, Q3, Q4, Q5, Q6, Q7, Q8, Q9, Q10, Q11, Q12, Q13, Q14, Q15, Q16, Q17, Q18, Q19, Q20, Q21, Q22, Q23, Q24, Q25, Q26, Q27, Q28, Q29, Q30, Q31, Q32, Q33, Q34, Q35, Q36, Q37, Q38, Q39, Q40, Q41, Q42, Q43, Q44, Q45]), "operationType" : NewBodyOperationType.ADD, "depth" : 2 * mm});
        }
        {
            var Q0;
            {var subQ0=sQuery(id+"F2.wireOp",EDGE,"E4");Q0=makeQuery(id+"F3.boolean.opBoolean","MERGE",FACE,{"derivedFrom":[makeQuery(id+"F1.opExtrude","CAP_FACE",FACE,{"disambiguationData":[OSD([sQuery(id+"F0.wireOp",EDGE,"E0")])],"isStart":false}),makeQuery(id+"F3.opExtrude","CAP_FACE",FACE,{"disambiguationData":[OSD([sQuery(id+"F2.wireOp",EDGE,"E2"),subQ0,sQuery(id+"F2.wireOp",EDGE,"E7"),sQuery(id+"F2.wireOp",EDGE,"E8"),sQuery(id+"F2.wireOp",EDGE,"E9"),sQuery(id+"F2.wireOp",EDGE,"E12")])],"isStart":false}),makeQuery(id+"F3.opExtrude","CAP_FACE",FACE,{"disambiguationData":[OSD([subQ0,sQuery(id+"F2.wireOp",EDGE,"E13.32.0"),sQuery(id+"F2.wireOp",EDGE,"E13.32.1"),sQuery(id+"F2.wireOp",EDGE,"E13.32.2"),sQuery(id+"F2.wireOp",EDGE,"E13.32.3"),sQuery(id+"F2.wireOp",EDGE,"E13.32.4")])],"isStart":false}),makeQuery(id+"F3.opExtrude","CAP_FACE",FACE,{"disambiguationData":[OSD([subQ0,sQuery(id+"F2.wireOp",EDGE,"E13.33.0"),sQuery(id+"F2.wireOp",EDGE,"E13.33.1"),sQuery(id+"F2.wireOp",EDGE,"E13.33.2"),sQuery(id+"F2.wireOp",EDGE,"E13.33.3"),sQuery(id+"F2.wireOp",EDGE,"E13.33.4")])],"isStart":false}),makeQuery(id+"F3.opExtrude","CAP_FACE",FACE,{"disambiguationData":[OSD([subQ0,sQuery(id+"F2.wireOp",EDGE,"E13.34.0"),sQuery(id+"F2.wireOp",EDGE,"E13.34.1"),sQuery(id+"F2.wireOp",EDGE,"E13.34.2"),sQuery(id+"F2.wireOp",EDGE,"E13.34.3"),sQuery(id+"F2.wireOp",EDGE,"E13.34.4")])],"isStart":false}),makeQuery(id+"F3.opExtrude","CAP_FACE",FACE,{"disambiguationData":[OSD([subQ0,sQuery(id+"F2.wireOp",EDGE,"E13.35.0"),sQuery(id+"F2.wireOp",EDGE,"E13.35.1"),sQuery(id+"F2.wireOp",EDGE,"E13.35.2"),sQuery(id+"F2.wireOp",EDGE,"E13.35.3"),sQuery(id+"F2.wireOp",EDGE,"E13.35.4")])],"isStart":false}),makeQuery(id+"F3.opExtrude","CAP_FACE",FACE,{"disambiguationData":[OSD([subQ0,sQuery(id+"F2.wireOp",EDGE,"E13.36.0"),sQuery(id+"F2.wireOp",EDGE,"E13.36.1"),sQuery(id+"F2.wireOp",EDGE,"E13.36.2"),sQuery(id+"F2.wireOp",EDGE,"E13.36.3"),sQuery(id+"F2.wireOp",EDGE,"E13.36.4")])],"isStart":false}),makeQuery(id+"F3.opExtrude","CAP_FACE",FACE,{"disambiguationData":[OSD([subQ0,sQuery(id+"F2.wireOp",EDGE,"E13.37.0"),sQuery(id+"F2.wireOp",EDGE,"E13.37.1"),sQuery(id+"F2.wireOp",EDGE,"E13.37.2"),sQuery(id+"F2.wireOp",EDGE,"E13.37.3"),sQuery(id+"F2.wireOp",EDGE,"E13.37.4")])],"isStart":false}),makeQuery(id+"F3.opExtrude","CAP_FACE",FACE,{"disambiguationData":[OSD([subQ0,sQuery(id+"F2.wireOp",EDGE,"E13.38.0"),sQuery(id+"F2.wireOp",EDGE,"E13.38.1"),sQuery(id+"F2.wireOp",EDGE,"E13.38.2"),sQuery(id+"F2.wireOp",EDGE,"E13.38.3"),sQuery(id+"F2.wireOp",EDGE,"E13.38.4")])],"isStart":false}),makeQuery(id+"F3.opExtrude","CAP_FACE",FACE,{"disambiguationData":[OSD([subQ0,sQuery(id+"F2.wireOp",EDGE,"E13.39.0"),sQuery(id+"F2.wireOp",EDGE,"E13.39.1"),sQuery(id+"F2.wireOp",EDGE,"E13.39.2"),sQuery(id+"F2.wireOp",EDGE,"E13.39.3"),sQuery(id+"F2.wireOp",EDGE,"E13.39.4")])],"isStart":false}),makeQuery(id+"F3.opExtrude","CAP_FACE",FACE,{"disambiguationData":[OSD([subQ0,sQuery(id+"F2.wireOp",EDGE,"E13.40.0"),sQuery(id+"F2.wireOp",EDGE,"E13.40.1"),sQuery(id+"F2.wireOp",EDGE,"E13.40.2"),sQuery(id+"F2.wireOp",EDGE,"E13.40.3"),sQuery(id+"F2.wireOp",EDGE,"E13.40.4")])],"isStart":false}),makeQuery(id+"F3.opExtrude","CAP_FACE",FACE,{"disambiguationData":[OSD([subQ0,sQuery(id+"F2.wireOp",EDGE,"E13.41.0"),sQuery(id+"F2.wireOp",EDGE,"E13.41.1"),sQuery(id+"F2.wireOp",EDGE,"E13.41.2"),sQuery(id+"F2.wireOp",EDGE,"E13.41.3"),sQuery(id+"F2.wireOp",EDGE,"E13.41.4")])],"isStart":false}),makeQuery(id+"F3.opExtrude","CAP_FACE",FACE,{"disambiguationData":[OSD([subQ0,sQuery(id+"F2.wireOp",EDGE,"E13.1.0"),sQuery(id+"F2.wireOp",EDGE,"E13.1.1"),sQuery(id+"F2.wireOp",EDGE,"E13.1.2"),sQuery(id+"F2.wireOp",EDGE,"E13.1.3"),sQuery(id+"F2.wireOp",EDGE,"E13.1.4")])],"isStart":false}),makeQuery(id+"F3.opExtrude","CAP_FACE",FACE,{"disambiguationData":[OSD([subQ0,sQuery(id+"F2.wireOp",EDGE,"E13.2.0"),sQuery(id+"F2.wireOp",EDGE,"E13.2.1"),sQuery(id+"F2.wireOp",EDGE,"E13.2.2"),sQuery(id+"F2.wireOp",EDGE,"E13.2.3"),sQuery(id+"F2.wireOp",EDGE,"E13.2.4")])],"isStart":false}),makeQuery(id+"F3.opExtrude","CAP_FACE",FACE,{"disambiguationData":[OSD([subQ0,sQuery(id+"F2.wireOp",EDGE,"E13.3.0"),sQuery(id+"F2.wireOp",EDGE,"E13.3.1"),sQuery(id+"F2.wireOp",EDGE,"E13.3.2"),sQuery(id+"F2.wireOp",EDGE,"E13.3.3"),sQuery(id+"F2.wireOp",EDGE,"E13.3.4")])],"isStart":false}),makeQuery(id+"F3.opExtrude","CAP_FACE",FACE,{"disambiguationData":[OSD([subQ0,sQuery(id+"F2.wireOp",EDGE,"E13.4.0"),sQuery(id+"F2.wireOp",EDGE,"E13.4.1"),sQuery(id+"F2.wireOp",EDGE,"E13.4.2"),sQuery(id+"F2.wireOp",EDGE,"E13.4.3"),sQuery(id+"F2.wireOp",EDGE,"E13.4.4")])],"isStart":false}),makeQuery(id+"F3.opExtrude","CAP_FACE",FACE,{"disambiguationData":[OSD([subQ0,sQuery(id+"F2.wireOp",EDGE,"E13.5.0"),sQuery(id+"F2.wireOp",EDGE,"E13.5.1"),sQuery(id+"F2.wireOp",EDGE,"E13.5.2"),sQuery(id+"F2.wireOp",EDGE,"E13.5.3"),sQuery(id+"F2.wireOp",EDGE,"E13.5.4")])],"isStart":false}),makeQuery(id+"F3.opExtrude","CAP_FACE",FACE,{"disambiguationData":[OSD([subQ0,sQuery(id+"F2.wireOp",EDGE,"E13.6.0"),sQuery(id+"F2.wireOp",EDGE,"E13.6.1"),sQuery(id+"F2.wireOp",EDGE,"E13.6.2"),sQuery(id+"F2.wireOp",EDGE,"E13.6.3"),sQuery(id+"F2.wireOp",EDGE,"E13.6.4")])],"isStart":false}),makeQuery(id+"F3.opExtrude","CAP_FACE",FACE,{"disambiguationData":[OSD([subQ0,sQuery(id+"F2.wireOp",EDGE,"E13.7.0"),sQuery(id+"F2.wireOp",EDGE,"E13.7.1"),sQuery(id+"F2.wireOp",EDGE,"E13.7.2"),sQuery(id+"F2.wireOp",EDGE,"E13.7.3"),sQuery(id+"F2.wireOp",EDGE,"E13.7.4")])],"isStart":false}),makeQuery(id+"F3.opExtrude","CAP_FACE",FACE,{"disambiguationData":[OSD([subQ0,sQuery(id+"F2.wireOp",EDGE,"E13.8.0"),sQuery(id+"F2.wireOp",EDGE,"E13.8.1"),sQuery(id+"F2.wireOp",EDGE,"E13.8.2"),sQuery(id+"F2.wireOp",EDGE,"E13.8.3"),sQuery(id+"F2.wireOp",EDGE,"E13.8.4")])],"isStart":false}),makeQuery(id+"F3.opExtrude","CAP_FACE",FACE,{"disambiguationData":[OSD([subQ0,sQuery(id+"F2.wireOp",EDGE,"E13.9.0"),sQuery(id+"F2.wireOp",EDGE,"E13.9.1"),sQuery(id+"F2.wireOp",EDGE,"E13.9.2"),sQuery(id+"F2.wireOp",EDGE,"E13.9.3"),sQuery(id+"F2.wireOp",EDGE,"E13.9.4")])],"isStart":false}),makeQuery(id+"F3.opExtrude","CAP_FACE",FACE,{"disambiguationData":[OSD([subQ0,sQuery(id+"F2.wireOp",EDGE,"E13.10.0"),sQuery(id+"F2.wireOp",EDGE,"E13.10.1"),sQuery(id+"F2.wireOp",EDGE,"E13.10.2"),sQuery(id+"F2.wireOp",EDGE,"E13.10.3"),sQuery(id+"F2.wireOp",EDGE,"E13.10.4")])],"isStart":false}),makeQuery(id+"F3.opExtrude","CAP_FACE",FACE,{"disambiguationData":[OSD([subQ0,sQuery(id+"F2.wireOp",EDGE,"E13.11.0"),sQuery(id+"F2.wireOp",EDGE,"E13.11.1"),sQuery(id+"F2.wireOp",EDGE,"E13.11.2"),sQuery(id+"F2.wireOp",EDGE,"E13.11.3"),sQuery(id+"F2.wireOp",EDGE,"E13.11.4")])],"isStart":false}),makeQuery(id+"F3.opExtrude","CAP_FACE",FACE,{"disambiguationData":[OSD([subQ0,sQuery(id+"F2.wireOp",EDGE,"E13.12.0"),sQuery(id+"F2.wireOp",EDGE,"E13.12.1"),sQuery(id+"F2.wireOp",EDGE,"E13.12.2"),sQuery(id+"F2.wireOp",EDGE,"E13.12.3"),sQuery(id+"F2.wireOp",EDGE,"E13.12.4")])],"isStart":false}),makeQuery(id+"F3.opExtrude","CAP_FACE",FACE,{"disambiguationData":[OSD([subQ0,sQuery(id+"F2.wireOp",EDGE,"E13.13.0"),sQuery(id+"F2.wireOp",EDGE,"E13.13.1"),sQuery(id+"F2.wireOp",EDGE,"E13.13.2"),sQuery(id+"F2.wireOp",EDGE,"E13.13.3"),sQuery(id+"F2.wireOp",EDGE,"E13.13.4")])],"isStart":false}),makeQuery(id+"F3.opExtrude","CAP_FACE",FACE,{"disambiguationData":[OSD([subQ0,sQuery(id+"F2.wireOp",EDGE,"E13.14.0"),sQuery(id+"F2.wireOp",EDGE,"E13.14.1"),sQuery(id+"F2.wireOp",EDGE,"E13.14.2"),sQuery(id+"F2.wireOp",EDGE,"E13.14.3"),sQuery(id+"F2.wireOp",EDGE,"E13.14.4")])],"isStart":false}),makeQuery(id+"F3.opExtrude","CAP_FACE",FACE,{"disambiguationData":[OSD([subQ0,sQuery(id+"F2.wireOp",EDGE,"E13.15.0"),sQuery(id+"F2.wireOp",EDGE,"E13.15.1"),sQuery(id+"F2.wireOp",EDGE,"E13.15.2"),sQuery(id+"F2.wireOp",EDGE,"E13.15.3"),sQuery(id+"F2.wireOp",EDGE,"E13.15.4")])],"isStart":false}),makeQuery(id+"F3.opExtrude","CAP_FACE",FACE,{"disambiguationData":[OSD([subQ0,sQuery(id+"F2.wireOp",EDGE,"E13.16.0"),sQuery(id+"F2.wireOp",EDGE,"E13.16.1"),sQuery(id+"F2.wireOp",EDGE,"E13.16.2"),sQuery(id+"F2.wireOp",EDGE,"E13.16.3"),sQuery(id+"F2.wireOp",EDGE,"E13.16.4")])],"isStart":false}),makeQuery(id+"F3.opExtrude","CAP_FACE",FACE,{"disambiguationData":[OSD([subQ0,sQuery(id+"F2.wireOp",EDGE,"E13.17.0"),sQuery(id+"F2.wireOp",EDGE,"E13.17.1"),sQuery(id+"F2.wireOp",EDGE,"E13.17.2"),sQuery(id+"F2.wireOp",EDGE,"E13.17.3"),sQuery(id+"F2.wireOp",EDGE,"E13.17.4")])],"isStart":false}),makeQuery(id+"F3.opExtrude","CAP_FACE",FACE,{"disambiguationData":[OSD([subQ0,sQuery(id+"F2.wireOp",EDGE,"E13.18.0"),sQuery(id+"F2.wireOp",EDGE,"E13.18.1"),sQuery(id+"F2.wireOp",EDGE,"E13.18.2"),sQuery(id+"F2.wireOp",EDGE,"E13.18.3"),sQuery(id+"F2.wireOp",EDGE,"E13.18.4")])],"isStart":false}),makeQuery(id+"F3.opExtrude","CAP_FACE",FACE,{"disambiguationData":[OSD([subQ0,sQuery(id+"F2.wireOp",EDGE,"E13.19.0"),sQuery(id+"F2.wireOp",EDGE,"E13.19.1"),sQuery(id+"F2.wireOp",EDGE,"E13.19.2"),sQuery(id+"F2.wireOp",EDGE,"E13.19.3"),sQuery(id+"F2.wireOp",EDGE,"E13.19.4")])],"isStart":false}),makeQuery(id+"F3.opExtrude","CAP_FACE",FACE,{"disambiguationData":[OSD([subQ0,sQuery(id+"F2.wireOp",EDGE,"E13.20.0"),sQuery(id+"F2.wireOp",EDGE,"E13.20.1"),sQuery(id+"F2.wireOp",EDGE,"E13.20.2"),sQuery(id+"F2.wireOp",EDGE,"E13.20.3"),sQuery(id+"F2.wireOp",EDGE,"E13.20.4")])],"isStart":false}),makeQuery(id+"F3.opExtrude","CAP_FACE",FACE,{"disambiguationData":[OSD([subQ0,sQuery(id+"F2.wireOp",EDGE,"E13.21.0"),sQuery(id+"F2.wireOp",EDGE,"E13.21.1"),sQuery(id+"F2.wireOp",EDGE,"E13.21.2"),sQuery(id+"F2.wireOp",EDGE,"E13.21.3"),sQuery(id+"F2.wireOp",EDGE,"E13.21.4")])],"isStart":false}),makeQuery(id+"F3.opExtrude","CAP_FACE",FACE,{"disambiguationData":[OSD([subQ0,sQuery(id+"F2.wireOp",EDGE,"E13.22.0"),sQuery(id+"F2.wireOp",EDGE,"E13.22.1"),sQuery(id+"F2.wireOp",EDGE,"E13.22.2"),sQuery(id+"F2.wireOp",EDGE,"E13.22.3"),sQuery(id+"F2.wireOp",EDGE,"E13.22.4")])],"isStart":false}),makeQuery(id+"F3.opExtrude","CAP_FACE",FACE,{"disambiguationData":[OSD([subQ0,sQuery(id+"F2.wireOp",EDGE,"E13.23.0"),sQuery(id+"F2.wireOp",EDGE,"E13.23.1"),sQuery(id+"F2.wireOp",EDGE,"E13.23.2"),sQuery(id+"F2.wireOp",EDGE,"E13.23.3"),sQuery(id+"F2.wireOp",EDGE,"E13.23.4")])],"isStart":false}),makeQuery(id+"F3.opExtrude","CAP_FACE",FACE,{"disambiguationData":[OSD([subQ0,sQuery(id+"F2.wireOp",EDGE,"E13.24.0"),sQuery(id+"F2.wireOp",EDGE,"E13.24.1"),sQuery(id+"F2.wireOp",EDGE,"E13.24.2"),sQuery(id+"F2.wireOp",EDGE,"E13.24.3"),sQuery(id+"F2.wireOp",EDGE,"E13.24.4")])],"isStart":false}),makeQuery(id+"F3.opExtrude","CAP_FACE",FACE,{"disambiguationData":[OSD([subQ0,sQuery(id+"F2.wireOp",EDGE,"E13.25.0"),sQuery(id+"F2.wireOp",EDGE,"E13.25.1"),sQuery(id+"F2.wireOp",EDGE,"E13.25.2"),sQuery(id+"F2.wireOp",EDGE,"E13.25.3"),sQuery(id+"F2.wireOp",EDGE,"E13.25.4")])],"isStart":false}),makeQuery(id+"F3.opExtrude","CAP_FACE",FACE,{"disambiguationData":[OSD([subQ0,sQuery(id+"F2.wireOp",EDGE,"E13.26.0"),sQuery(id+"F2.wireOp",EDGE,"E13.26.1"),sQuery(id+"F2.wireOp",EDGE,"E13.26.2"),sQuery(id+"F2.wireOp",EDGE,"E13.26.3"),sQuery(id+"F2.wireOp",EDGE,"E13.26.4")])],"isStart":false}),makeQuery(id+"F3.opExtrude","CAP_FACE",FACE,{"disambiguationData":[OSD([subQ0,sQuery(id+"F2.wireOp",EDGE,"E13.27.0"),sQuery(id+"F2.wireOp",EDGE,"E13.27.1"),sQuery(id+"F2.wireOp",EDGE,"E13.27.2"),sQuery(id+"F2.wireOp",EDGE,"E13.27.3"),sQuery(id+"F2.wireOp",EDGE,"E13.27.4")])],"isStart":false}),makeQuery(id+"F3.opExtrude","CAP_FACE",FACE,{"disambiguationData":[OSD([subQ0,sQuery(id+"F2.wireOp",EDGE,"E13.28.0"),sQuery(id+"F2.wireOp",EDGE,"E13.28.1"),sQuery(id+"F2.wireOp",EDGE,"E13.28.2"),sQuery(id+"F2.wireOp",EDGE,"E13.28.3"),sQuery(id+"F2.wireOp",EDGE,"E13.28.4")])],"isStart":false}),makeQuery(id+"F3.opExtrude","CAP_FACE",FACE,{"disambiguationData":[OSD([subQ0,sQuery(id+"F2.wireOp",EDGE,"E13.29.0"),sQuery(id+"F2.wireOp",EDGE,"E13.29.1"),sQuery(id+"F2.wireOp",EDGE,"E13.29.2"),sQuery(id+"F2.wireOp",EDGE,"E13.29.3"),sQuery(id+"F2.wireOp",EDGE,"E13.29.4")])],"isStart":false}),makeQuery(id+"F3.opExtrude","CAP_FACE",FACE,{"disambiguationData":[OSD([subQ0,sQuery(id+"F2.wireOp",EDGE,"E13.30.0"),sQuery(id+"F2.wireOp",EDGE,"E13.30.1"),sQuery(id+"F2.wireOp",EDGE,"E13.30.2"),sQuery(id+"F2.wireOp",EDGE,"E13.30.3"),sQuery(id+"F2.wireOp",EDGE,"E13.30.4")])],"isStart":false}),makeQuery(id+"F3.opExtrude","CAP_FACE",FACE,{"disambiguationData":[OSD([subQ0,sQuery(id+"F2.wireOp",EDGE,"E13.31.0"),sQuery(id+"F2.wireOp",EDGE,"E13.31.1"),sQuery(id+"F2.wireOp",EDGE,"E13.31.2"),sQuery(id+"F2.wireOp",EDGE,"E13.31.3"),sQuery(id+"F2.wireOp",EDGE,"E13.31.4")])],"isStart":false})]});}
            var sketch = newSketch(context, id + "F4", { "sketchPlane" : qUnion([Q0])});
            skCircle(sketch, "E14", {"center": v(0, 0) * mm, "radius": 9 * mm});
            skSolve(sketch);
        }
        {
            var Q0;
            Q0 = qSketchRegion(id + "F4", true);
            extrude(context, id + "F5", {"entities" : qUnion([Q0]), "operationType" : NewBodyOperationType.REMOVE, "oppositeDirection" : true, "depth" : 0.2 * mm});
        }
        {
            var Q0;
            Q0=makeQuery(id+"F5.boolean.opBoolean","COPY",FACE,{"derivedFrom":makeQuery(id+"F5.opExtrude","CAP_FACE",FACE,{"disambiguationData":[OSD([sQuery(id+"F4.wireOp",EDGE,"E14")])],"isStart":false})});
            var sketch = newSketch(context, id + "F6", { "sketchPlane" : qUnion([Q0])});
            skCircle(sketch, "E15", {"center": v(0, 0) * mm, "radius": 2.38 * mm});
            skArc(sketch, "E16", {"start": v(0.4, 2.97) * mm, "mid": v(0, 3) * mm, "end": v(-0.4, 2.97) * mm});
            skArc(sketch, "E17", {"start": v(0.26, 3.5) * mm, "mid": v(-0.1, 3.5) * mm, "end": v(-0.46, 3.47) * mm});
            skArc(sketch, "E18", {"start": v(0, 4.5) * mm, "mid": v(-0.3, 4.5) * mm, "end": v(-0.59, 4.46) * mm});
            skLineSegment(sketch, "E19", {"start": v(0, 0) * mm, "end": v(0, 5.48) * mm});
            skPoint(sketch, "E20.startSnap0", {"position": v(0, 2.74) * mm});
            skPoint(sketch, "E20.endSnap0", {"position": v(-0.4, 2.97) * mm});
            skLineSegment(sketch, "E21", {"start": v(0, 0) * mm, "end": v(-0.3, 2.35) * mm});
            skLineSegment(sketch, "E22", {"start": v(-0.3, 2.35) * mm, "end": v(-0.4, 2.97) * mm});
            skLineSegment(sketch, "E23", {"start": v(-0.4, 2.97) * mm, "end": v(-0.46, 3.47) * mm});
            skLineSegment(sketch, "E24", {"start": v(-0.46, 3.47) * mm, "end": v(-0.59, 4.46) * mm});
            skLineSegment(sketch, "E25", {"start": v(-0.59, 4.46) * mm, "end": v(-0.66, 4.98) * mm});
            skLineSegment(sketch, "E26", {"start": v(0, 4.5) * mm, "end": v(-0.26, 3.5) * mm});
            skLineSegment(sketch, "E27", {"start": v(-0.26, 3.5) * mm, "end": v(-0.4, 2.97) * mm});
            skLineSegment(sketch, "E28", {"start": v(0, 4.5) * mm, "end": v(0.26, 3.5) * mm});
            skLineSegment(sketch, "E29", {"start": v(0.26, 3.5) * mm, "end": v(0.4, 2.97) * mm});
            skLineSegment(sketch, "E30", {"start": v(0.4, 2.97) * mm, "end": v(0.3, 2.35) * mm});
            skLineSegment(sketch, "E31", {"start": v(0.3, 2.35) * mm, "end": v(0, 0) * mm});
            skLineSegment(sketch, "E32.1.0", {"start": v(-1.45, 1.88) * mm, "end": v(-1.83, 2.38) * mm});
            skLineSegment(sketch, "E32.1.1", {"start": v(-1.97, 2.9) * mm, "end": v(-1.83, 2.38) * mm});
            skArc(sketch, "E32.1.2", {"start": v(-1.52, 3.15) * mm, "mid": v(-1.84, 2.98) * mm, "end": v(-2.13, 2.78) * mm});
            skLineSegment(sketch, "E32.1.3", {"start": v(-1.52, 3.15) * mm, "end": v(-1.15, 2.77) * mm});
            skLineSegment(sketch, "E32.1.4", {"start": v(-1.15, 2.77) * mm, "end": v(-0.9, 2.2) * mm});
            skLineSegment(sketch, "E32.2.0", {"start": v(-2.2, 0.9) * mm, "end": v(-2.77, 1.15) * mm});
            skLineSegment(sketch, "E32.2.1", {"start": v(-3.15, 1.52) * mm, "end": v(-2.77, 1.15) * mm});
            skArc(sketch, "E32.2.2", {"start": v(-2.9, 1.97) * mm, "mid": v(-3.08, 1.66) * mm, "end": v(-3.23, 1.34) * mm});
            skLineSegment(sketch, "E32.2.3", {"start": v(-2.9, 1.97) * mm, "end": v(-2.38, 1.83) * mm});
            skLineSegment(sketch, "E32.2.4", {"start": v(-2.38, 1.83) * mm, "end": v(-1.88, 1.45) * mm});
            skLineSegment(sketch, "E32.3.0", {"start": v(-2.35, -0.3) * mm, "end": v(-2.97, -0.4) * mm});
            skLineSegment(sketch, "E32.3.1", {"start": v(-3.5, -0.26) * mm, "end": v(-2.97, -0.4) * mm});
            skArc(sketch, "E32.3.2", {"start": v(-3.5, 0.26) * mm, "mid": v(-3.5, -0.1) * mm, "end": v(-3.47, -0.46) * mm});
            skLineSegment(sketch, "E32.3.3", {"start": v(-3.5, 0.26) * mm, "end": v(-2.97, 0.4) * mm});
            skLineSegment(sketch, "E32.3.4", {"start": v(-2.97, 0.4) * mm, "end": v(-2.35, 0.3) * mm});
            skLineSegment(sketch, "E32.4.0", {"start": v(-1.88, -1.45) * mm, "end": v(-2.38, -1.83) * mm});
            skLineSegment(sketch, "E32.4.1", {"start": v(-2.9, -1.97) * mm, "end": v(-2.38, -1.83) * mm});
            skArc(sketch, "E32.4.2", {"start": v(-3.15, -1.52) * mm, "mid": v(-2.98, -1.84) * mm, "end": v(-2.78, -2.13) * mm});
            skLineSegment(sketch, "E32.4.3", {"start": v(-3.15, -1.52) * mm, "end": v(-2.77, -1.15) * mm});
            skLineSegment(sketch, "E32.4.4", {"start": v(-2.77, -1.15) * mm, "end": v(-2.2, -0.9) * mm});
            skLineSegment(sketch, "E32.5.0", {"start": v(-0.9, -2.2) * mm, "end": v(-1.15, -2.77) * mm});
            skLineSegment(sketch, "E32.5.1", {"start": v(-1.52, -3.15) * mm, "end": v(-1.15, -2.77) * mm});
            skArc(sketch, "E32.5.2", {"start": v(-1.97, -2.9) * mm, "mid": v(-1.66, -3.08) * mm, "end": v(-1.34, -3.23) * mm});
            skLineSegment(sketch, "E32.5.3", {"start": v(-1.97, -2.9) * mm, "end": v(-1.83, -2.38) * mm});
            skLineSegment(sketch, "E32.5.4", {"start": v(-1.83, -2.38) * mm, "end": v(-1.45, -1.88) * mm});
            skLineSegment(sketch, "E32.6.0", {"start": v(0.3, -2.35) * mm, "end": v(0.4, -2.97) * mm});
            skLineSegment(sketch, "E32.6.1", {"start": v(0.26, -3.5) * mm, "end": v(0.4, -2.97) * mm});
            skArc(sketch, "E32.6.2", {"start": v(-0.26, -3.5) * mm, "mid": v(0.1, -3.5) * mm, "end": v(0.46, -3.47) * mm});
            skLineSegment(sketch, "E32.6.3", {"start": v(-0.26, -3.5) * mm, "end": v(-0.4, -2.97) * mm});
            skLineSegment(sketch, "E32.6.4", {"start": v(-0.4, -2.97) * mm, "end": v(-0.3, -2.35) * mm});
            skLineSegment(sketch, "E32.7.0", {"start": v(1.45, -1.88) * mm, "end": v(1.83, -2.38) * mm});
            skLineSegment(sketch, "E32.7.1", {"start": v(1.97, -2.9) * mm, "end": v(1.83, -2.38) * mm});
            skArc(sketch, "E32.7.2", {"start": v(1.52, -3.15) * mm, "mid": v(1.84, -2.98) * mm, "end": v(2.13, -2.78) * mm});
            skLineSegment(sketch, "E32.7.3", {"start": v(1.52, -3.15) * mm, "end": v(1.15, -2.77) * mm});
            skLineSegment(sketch, "E32.7.4", {"start": v(1.15, -2.77) * mm, "end": v(0.9, -2.2) * mm});
            skLineSegment(sketch, "E32.8.0", {"start": v(2.2, -0.9) * mm, "end": v(2.77, -1.15) * mm});
            skLineSegment(sketch, "E32.8.1", {"start": v(3.15, -1.52) * mm, "end": v(2.77, -1.15) * mm});
            skArc(sketch, "E32.8.2", {"start": v(2.9, -1.97) * mm, "mid": v(3.08, -1.66) * mm, "end": v(3.23, -1.34) * mm});
            skLineSegment(sketch, "E32.8.3", {"start": v(2.9, -1.97) * mm, "end": v(2.38, -1.83) * mm});
            skLineSegment(sketch, "E32.8.4", {"start": v(2.38, -1.83) * mm, "end": v(1.88, -1.45) * mm});
            skLineSegment(sketch, "E32.9.0", {"start": v(2.35, 0.3) * mm, "end": v(2.97, 0.4) * mm});
            skLineSegment(sketch, "E32.9.1", {"start": v(3.5, 0.26) * mm, "end": v(2.97, 0.4) * mm});
            skArc(sketch, "E32.9.2", {"start": v(3.5, -0.26) * mm, "mid": v(3.5, 0.1) * mm, "end": v(3.47, 0.46) * mm});
            skLineSegment(sketch, "E32.9.3", {"start": v(3.5, -0.26) * mm, "end": v(2.97, -0.4) * mm});
            skLineSegment(sketch, "E32.9.4", {"start": v(2.97, -0.4) * mm, "end": v(2.35, -0.3) * mm});
            skLineSegment(sketch, "E32.10.0", {"start": v(1.88, 1.45) * mm, "end": v(2.38, 1.83) * mm});
            skLineSegment(sketch, "E32.10.1", {"start": v(2.9, 1.97) * mm, "end": v(2.38, 1.83) * mm});
            skArc(sketch, "E32.10.2", {"start": v(3.15, 1.52) * mm, "mid": v(2.98, 1.84) * mm, "end": v(2.78, 2.13) * mm});
            skLineSegment(sketch, "E32.10.3", {"start": v(3.15, 1.52) * mm, "end": v(2.77, 1.15) * mm});
            skLineSegment(sketch, "E32.10.4", {"start": v(2.77, 1.15) * mm, "end": v(2.2, 0.9) * mm});
            skLineSegment(sketch, "E32.11.0", {"start": v(0.9, 2.2) * mm, "end": v(1.15, 2.77) * mm});
            skLineSegment(sketch, "E32.11.1", {"start": v(1.52, 3.15) * mm, "end": v(1.15, 2.77) * mm});
            skArc(sketch, "E32.11.2", {"start": v(1.97, 2.9) * mm, "mid": v(1.66, 3.08) * mm, "end": v(1.34, 3.23) * mm});
            skLineSegment(sketch, "E32.11.3", {"start": v(1.97, 2.9) * mm, "end": v(1.83, 2.38) * mm});
            skLineSegment(sketch, "E32.11.4", {"start": v(1.83, 2.38) * mm, "end": v(1.45, 1.88) * mm});
            skSolve(sketch);
        }
        {
            var Q0;
            {var subQ3=sQuery(id+"F6.wireOp",EDGE,"E32.10.0");Q0=makeQuery(id+"F6.imprint","IMPRINT",FACE,{"disambiguationData":[TD([[makeQuery(id+"F6.imprint","IMPRINT",EDGE,{"derivedFrom":subQ3}),-1.0]])]});}
            var Q1;
            {var subQ3=sQuery(id+"F6.wireOp",EDGE,"E32.11.0");Q1=makeQuery(id+"F6.imprint","IMPRINT",FACE,{"disambiguationData":[TD([[makeQuery(id+"F6.imprint","IMPRINT",EDGE,{"derivedFrom":subQ3}),-1.0]])]});}
            var Q2;
            {var subQ3=sQuery(id+"F6.wireOp",EDGE,"E32.1.0");Q2=makeQuery(id+"F6.imprint","IMPRINT",FACE,{"disambiguationData":[TD([[makeQuery(id+"F6.imprint","IMPRINT",EDGE,{"derivedFrom":subQ3}),-1.0]])]});}
            var Q3;
            {var subQ3=sQuery(id+"F6.wireOp",EDGE,"E32.2.0");Q3=makeQuery(id+"F6.imprint","IMPRINT",FACE,{"disambiguationData":[TD([[makeQuery(id+"F6.imprint","IMPRINT",EDGE,{"derivedFrom":subQ3}),-1.0]])]});}
            var Q4;
            {var subQ1=sQuery(id+"F6.wireOp",EDGE,"E32.3.0");Q4=makeQuery(id+"F6.imprint","IMPRINT",FACE,{"disambiguationData":[TD([[makeQuery(id+"F6.imprint","IMPRINT",EDGE,{"derivedFrom":subQ1}),-1.0]])]});}
            var Q5;
            {var subQ3=sQuery(id+"F6.wireOp",EDGE,"E32.4.0");Q5=makeQuery(id+"F6.imprint","IMPRINT",FACE,{"disambiguationData":[TD([[makeQuery(id+"F6.imprint","IMPRINT",EDGE,{"derivedFrom":subQ3}),-1.0]])]});}
            var Q6;
            {var subQ3=sQuery(id+"F6.wireOp",EDGE,"E32.5.0");Q6=makeQuery(id+"F6.imprint","IMPRINT",FACE,{"disambiguationData":[TD([[makeQuery(id+"F6.imprint","IMPRINT",EDGE,{"derivedFrom":subQ3}),-1.0]])]});}
            var Q7;
            {var subQ3=sQuery(id+"F6.wireOp",EDGE,"E32.6.0");Q7=makeQuery(id+"F6.imprint","IMPRINT",FACE,{"disambiguationData":[TD([[makeQuery(id+"F6.imprint","IMPRINT",EDGE,{"derivedFrom":subQ3}),-1.0]])]});}
            var Q8;
            {var subQ3=sQuery(id+"F6.wireOp",EDGE,"E32.7.0");Q8=makeQuery(id+"F6.imprint","IMPRINT",FACE,{"disambiguationData":[TD([[makeQuery(id+"F6.imprint","IMPRINT",EDGE,{"derivedFrom":subQ3}),-1.0]])]});}
            var Q9;
            {var subQ1=sQuery(id+"F6.wireOp",EDGE,"E32.8.0");Q9=makeQuery(id+"F6.imprint","IMPRINT",FACE,{"disambiguationData":[TD([[makeQuery(id+"F6.imprint","IMPRINT",EDGE,{"derivedFrom":subQ1}),-1.0]])]});}
            var Q10;
            {var subQ3=sQuery(id+"F6.wireOp",EDGE,"E32.9.0");Q10=makeQuery(id+"F6.imprint","IMPRINT",FACE,{"disambiguationData":[TD([[makeQuery(id+"F6.imprint","IMPRINT",EDGE,{"derivedFrom":subQ3}),-1.0]])]});}
            var Q11;
            {var subQ0=sQuery(id+"F6.wireOp",EDGE,"E31");Q11=makeQuery(id+"F6.imprint","IMPRINT",FACE,{"disambiguationData":[TD([[makeQuery(id+"F6.imprint","IMPRINT",EDGE,{"derivedFrom":subQ0}),-1.0]])]});}
            var Q12;
            {var subQ0=sQuery(id+"F6.wireOp",EDGE,"E21");Q12=makeQuery(id+"F6.imprint","IMPRINT",FACE,{"disambiguationData":[TD([[makeQuery(id+"F6.imprint","IMPRINT",EDGE,{"derivedFrom":subQ0}),-1.0]])]});}
            var Q13;
            {var subQ0=sQuery(id+"F6.wireOp",EDGE,"E30");Q13=makeQuery(id+"F6.imprint","IMPRINT",FACE,{"disambiguationData":[TD([[makeQuery(id+"F6.imprint","IMPRINT",EDGE,{"derivedFrom":subQ0}),-1.0]])]});}
            var Q14;
            {var subQ0=sQuery(id+"F6.wireOp",EDGE,"E22");Q14=makeQuery(id+"F6.imprint","IMPRINT",FACE,{"disambiguationData":[TD([[makeQuery(id+"F6.imprint","IMPRINT",EDGE,{"derivedFrom":subQ0}),-1.0]])]});}
            var Q15;
            {var subQ0=sQuery(id+"F6.wireOp",EDGE,"E29");Q15=makeQuery(id+"F6.imprint","IMPRINT",FACE,{"disambiguationData":[TD([[makeQuery(id+"F6.imprint","IMPRINT",EDGE,{"derivedFrom":subQ0}),-1.0]])]});}
            var Q16;
            {var subQ0=sQuery(id+"F6.wireOp",EDGE,"E27");Q16=makeQuery(id+"F6.imprint","IMPRINT",FACE,{"disambiguationData":[TD([[makeQuery(id+"F6.imprint","IMPRINT",EDGE,{"derivedFrom":subQ0}),1.0]])]});}
            var Q17;
            {var subQ21=sQuery(id+"F6.wireOp",EDGE,"E21");Q17=makeQuery(id+"F6.imprint","IMPRINT",FACE,{"disambiguationData":[TD([[makeQuery(id+"F6.imprint","IMPRINT",EDGE,{"derivedFrom":subQ21}),1.0]])]});}
            extrude(context, id + "F7", {"entities" : qUnion([Q0, Q1, Q2, Q3, Q4, Q5, Q6, Q7, Q8, Q9, Q10, Q11, Q12, Q13, Q14, Q15, Q16, Q17]), "operationType" : NewBodyOperationType.ADD, "depth" : 4.9 * mm});
        }
        {
            var Q0;
            Q0=makeQuery(id+"F7.opExtrude","CAP_FACE",FACE,{"disambiguationData":[OSD([sQuery(id+"F6.wireOp",EDGE,"E15"),sQuery(id+"F6.wireOp",EDGE,"E17"),sQuery(id+"F6.wireOp",EDGE,"E22"),sQuery(id+"F6.wireOp",EDGE,"E27"),sQuery(id+"F6.wireOp",EDGE,"E29"),sQuery(id+"F6.wireOp",EDGE,"E30"),sQuery(id+"F6.wireOp",EDGE,"E32.1.0"),sQuery(id+"F6.wireOp",EDGE,"E32.1.1"),sQuery(id+"F6.wireOp",EDGE,"E32.1.2"),sQuery(id+"F6.wireOp",EDGE,"E32.1.3"),sQuery(id+"F6.wireOp",EDGE,"E32.1.4"),sQuery(id+"F6.wireOp",EDGE,"E32.2.0"),sQuery(id+"F6.wireOp",EDGE,"E32.2.1"),sQuery(id+"F6.wireOp",EDGE,"E32.2.2"),sQuery(id+"F6.wireOp",EDGE,"E32.2.3"),sQuery(id+"F6.wireOp",EDGE,"E32.2.4"),sQuery(id+"F6.wireOp",EDGE,"E32.3.0"),sQuery(id+"F6.wireOp",EDGE,"E32.3.1"),sQuery(id+"F6.wireOp",EDGE,"E32.3.2"),sQuery(id+"F6.wireOp",EDGE,"E32.3.3"),sQuery(id+"F6.wireOp",EDGE,"E32.3.4"),sQuery(id+"F6.wireOp",EDGE,"E32.4.0"),sQuery(id+"F6.wireOp",EDGE,"E32.4.1"),sQuery(id+"F6.wireOp",EDGE,"E32.4.2"),sQuery(id+"F6.wireOp",EDGE,"E32.4.3"),sQuery(id+"F6.wireOp",EDGE,"E32.4.4"),sQuery(id+"F6.wireOp",EDGE,"E32.5.0"),sQuery(id+"F6.wireOp",EDGE,"E32.5.1"),sQuery(id+"F6.wireOp",EDGE,"E32.5.2"),sQuery(id+"F6.wireOp",EDGE,"E32.5.3"),sQuery(id+"F6.wireOp",EDGE,"E32.5.4"),sQuery(id+"F6.wireOp",EDGE,"E32.6.0"),sQuery(id+"F6.wireOp",EDGE,"E32.6.1"),sQuery(id+"F6.wireOp",EDGE,"E32.6.2"),sQuery(id+"F6.wireOp",EDGE,"E32.6.3"),sQuery(id+"F6.wireOp",EDGE,"E32.6.4"),sQuery(id+"F6.wireOp",EDGE,"E32.7.0"),sQuery(id+"F6.wireOp",EDGE,"E32.7.1"),sQuery(id+"F6.wireOp",EDGE,"E32.7.2"),sQuery(id+"F6.wireOp",EDGE,"E32.7.3"),sQuery(id+"F6.wireOp",EDGE,"E32.7.4"),sQuery(id+"F6.wireOp",EDGE,"E32.8.0"),sQuery(id+"F6.wireOp",EDGE,"E32.8.1"),sQuery(id+"F6.wireOp",EDGE,"E32.8.2"),sQuery(id+"F6.wireOp",EDGE,"E32.8.3"),sQuery(id+"F6.wireOp",EDGE,"E32.8.4"),sQuery(id+"F6.wireOp",EDGE,"E32.9.0"),sQuery(id+"F6.wireOp",EDGE,"E32.9.1"),sQuery(id+"F6.wireOp",EDGE,"E32.9.2"),sQuery(id+"F6.wireOp",EDGE,"E32.9.3"),sQuery(id+"F6.wireOp",EDGE,"E32.9.4"),sQuery(id+"F6.wireOp",EDGE,"E32.10.0"),sQuery(id+"F6.wireOp",EDGE,"E32.10.1"),sQuery(id+"F6.wireOp",EDGE,"E32.10.2"),sQuery(id+"F6.wireOp",EDGE,"E32.10.3"),sQuery(id+"F6.wireOp",EDGE,"E32.10.4"),sQuery(id+"F6.wireOp",EDGE,"E32.11.0"),sQuery(id+"F6.wireOp",EDGE,"E32.11.1"),sQuery(id+"F6.wireOp",EDGE,"E32.11.2"),sQuery(id+"F6.wireOp",EDGE,"E32.11.3"),sQuery(id+"F6.wireOp",EDGE,"E32.11.4")])],"isStart":false});
            var sketch = newSketch(context, id + "F8", { "sketchPlane" : qUnion([Q0])});
            skCircle(sketch, "E33", {"center": v(0, 0) * mm, "radius": 2 * mm});
            skSolve(sketch);
        }
        {
            var Q0;
            Q0 = qSketchRegion(id + "F8", true);
            extrude(context, id + "F9", {"entities" : qUnion([Q0]), "operationType" : NewBodyOperationType.ADD, "depth" : 0.1 * mm});
        }
        {
            var Q0;
            {var subQ0=sQuery(id+"F2.wireOp",EDGE,"E4");Q0=makeQuery(id+"F3.boolean.opBoolean","MERGE",FACE,{"derivedFrom":[makeQuery(id+"F1.opExtrude","CAP_FACE",FACE,{"disambiguationData":[OSD([sQuery(id+"F0.wireOp",EDGE,"E0")])],"isStart":true}),makeQuery(id+"F3.opExtrude","CAP_FACE",FACE,{"disambiguationData":[OSD([sQuery(id+"F2.wireOp",EDGE,"E2"),subQ0,sQuery(id+"F2.wireOp",EDGE,"E7"),sQuery(id+"F2.wireOp",EDGE,"E8"),sQuery(id+"F2.wireOp",EDGE,"E9"),sQuery(id+"F2.wireOp",EDGE,"E12")])],"isStart":true}),makeQuery(id+"F3.opExtrude","CAP_FACE",FACE,{"disambiguationData":[OSD([subQ0,sQuery(id+"F2.wireOp",EDGE,"E13.32.0"),sQuery(id+"F2.wireOp",EDGE,"E13.32.1"),sQuery(id+"F2.wireOp",EDGE,"E13.32.2"),sQuery(id+"F2.wireOp",EDGE,"E13.32.3"),sQuery(id+"F2.wireOp",EDGE,"E13.32.4")])],"isStart":true}),makeQuery(id+"F3.opExtrude","CAP_FACE",FACE,{"disambiguationData":[OSD([subQ0,sQuery(id+"F2.wireOp",EDGE,"E13.33.0"),sQuery(id+"F2.wireOp",EDGE,"E13.33.1"),sQuery(id+"F2.wireOp",EDGE,"E13.33.2"),sQuery(id+"F2.wireOp",EDGE,"E13.33.3"),sQuery(id+"F2.wireOp",EDGE,"E13.33.4")])],"isStart":true}),makeQuery(id+"F3.opExtrude","CAP_FACE",FACE,{"disambiguationData":[OSD([subQ0,sQuery(id+"F2.wireOp",EDGE,"E13.34.0"),sQuery(id+"F2.wireOp",EDGE,"E13.34.1"),sQuery(id+"F2.wireOp",EDGE,"E13.34.2"),sQuery(id+"F2.wireOp",EDGE,"E13.34.3"),sQuery(id+"F2.wireOp",EDGE,"E13.34.4")])],"isStart":true}),makeQuery(id+"F3.opExtrude","CAP_FACE",FACE,{"disambiguationData":[OSD([subQ0,sQuery(id+"F2.wireOp",EDGE,"E13.35.0"),sQuery(id+"F2.wireOp",EDGE,"E13.35.1"),sQuery(id+"F2.wireOp",EDGE,"E13.35.2"),sQuery(id+"F2.wireOp",EDGE,"E13.35.3"),sQuery(id+"F2.wireOp",EDGE,"E13.35.4")])],"isStart":true}),makeQuery(id+"F3.opExtrude","CAP_FACE",FACE,{"disambiguationData":[OSD([subQ0,sQuery(id+"F2.wireOp",EDGE,"E13.36.0"),sQuery(id+"F2.wireOp",EDGE,"E13.36.1"),sQuery(id+"F2.wireOp",EDGE,"E13.36.2"),sQuery(id+"F2.wireOp",EDGE,"E13.36.3"),sQuery(id+"F2.wireOp",EDGE,"E13.36.4")])],"isStart":true}),makeQuery(id+"F3.opExtrude","CAP_FACE",FACE,{"disambiguationData":[OSD([subQ0,sQuery(id+"F2.wireOp",EDGE,"E13.37.0"),sQuery(id+"F2.wireOp",EDGE,"E13.37.1"),sQuery(id+"F2.wireOp",EDGE,"E13.37.2"),sQuery(id+"F2.wireOp",EDGE,"E13.37.3"),sQuery(id+"F2.wireOp",EDGE,"E13.37.4")])],"isStart":true}),makeQuery(id+"F3.opExtrude","CAP_FACE",FACE,{"disambiguationData":[OSD([subQ0,sQuery(id+"F2.wireOp",EDGE,"E13.38.0"),sQuery(id+"F2.wireOp",EDGE,"E13.38.1"),sQuery(id+"F2.wireOp",EDGE,"E13.38.2"),sQuery(id+"F2.wireOp",EDGE,"E13.38.3"),sQuery(id+"F2.wireOp",EDGE,"E13.38.4")])],"isStart":true}),makeQuery(id+"F3.opExtrude","CAP_FACE",FACE,{"disambiguationData":[OSD([subQ0,sQuery(id+"F2.wireOp",EDGE,"E13.39.0"),sQuery(id+"F2.wireOp",EDGE,"E13.39.1"),sQuery(id+"F2.wireOp",EDGE,"E13.39.2"),sQuery(id+"F2.wireOp",EDGE,"E13.39.3"),sQuery(id+"F2.wireOp",EDGE,"E13.39.4")])],"isStart":true}),makeQuery(id+"F3.opExtrude","CAP_FACE",FACE,{"disambiguationData":[OSD([subQ0,sQuery(id+"F2.wireOp",EDGE,"E13.40.0"),sQuery(id+"F2.wireOp",EDGE,"E13.40.1"),sQuery(id+"F2.wireOp",EDGE,"E13.40.2"),sQuery(id+"F2.wireOp",EDGE,"E13.40.3"),sQuery(id+"F2.wireOp",EDGE,"E13.40.4")])],"isStart":true}),makeQuery(id+"F3.opExtrude","CAP_FACE",FACE,{"disambiguationData":[OSD([subQ0,sQuery(id+"F2.wireOp",EDGE,"E13.41.0"),sQuery(id+"F2.wireOp",EDGE,"E13.41.1"),sQuery(id+"F2.wireOp",EDGE,"E13.41.2"),sQuery(id+"F2.wireOp",EDGE,"E13.41.3"),sQuery(id+"F2.wireOp",EDGE,"E13.41.4")])],"isStart":true}),makeQuery(id+"F3.opExtrude","CAP_FACE",FACE,{"disambiguationData":[OSD([subQ0,sQuery(id+"F2.wireOp",EDGE,"E13.1.0"),sQuery(id+"F2.wireOp",EDGE,"E13.1.1"),sQuery(id+"F2.wireOp",EDGE,"E13.1.2"),sQuery(id+"F2.wireOp",EDGE,"E13.1.3"),sQuery(id+"F2.wireOp",EDGE,"E13.1.4")])],"isStart":true}),makeQuery(id+"F3.opExtrude","CAP_FACE",FACE,{"disambiguationData":[OSD([subQ0,sQuery(id+"F2.wireOp",EDGE,"E13.2.0"),sQuery(id+"F2.wireOp",EDGE,"E13.2.1"),sQuery(id+"F2.wireOp",EDGE,"E13.2.2"),sQuery(id+"F2.wireOp",EDGE,"E13.2.3"),sQuery(id+"F2.wireOp",EDGE,"E13.2.4")])],"isStart":true}),makeQuery(id+"F3.opExtrude","CAP_FACE",FACE,{"disambiguationData":[OSD([subQ0,sQuery(id+"F2.wireOp",EDGE,"E13.3.0"),sQuery(id+"F2.wireOp",EDGE,"E13.3.1"),sQuery(id+"F2.wireOp",EDGE,"E13.3.2"),sQuery(id+"F2.wireOp",EDGE,"E13.3.3"),sQuery(id+"F2.wireOp",EDGE,"E13.3.4")])],"isStart":true}),makeQuery(id+"F3.opExtrude","CAP_FACE",FACE,{"disambiguationData":[OSD([subQ0,sQuery(id+"F2.wireOp",EDGE,"E13.4.0"),sQuery(id+"F2.wireOp",EDGE,"E13.4.1"),sQuery(id+"F2.wireOp",EDGE,"E13.4.2"),sQuery(id+"F2.wireOp",EDGE,"E13.4.3"),sQuery(id+"F2.wireOp",EDGE,"E13.4.4")])],"isStart":true}),makeQuery(id+"F3.opExtrude","CAP_FACE",FACE,{"disambiguationData":[OSD([subQ0,sQuery(id+"F2.wireOp",EDGE,"E13.5.0"),sQuery(id+"F2.wireOp",EDGE,"E13.5.1"),sQuery(id+"F2.wireOp",EDGE,"E13.5.2"),sQuery(id+"F2.wireOp",EDGE,"E13.5.3"),sQuery(id+"F2.wireOp",EDGE,"E13.5.4")])],"isStart":true}),makeQuery(id+"F3.opExtrude","CAP_FACE",FACE,{"disambiguationData":[OSD([subQ0,sQuery(id+"F2.wireOp",EDGE,"E13.6.0"),sQuery(id+"F2.wireOp",EDGE,"E13.6.1"),sQuery(id+"F2.wireOp",EDGE,"E13.6.2"),sQuery(id+"F2.wireOp",EDGE,"E13.6.3"),sQuery(id+"F2.wireOp",EDGE,"E13.6.4")])],"isStart":true}),makeQuery(id+"F3.opExtrude","CAP_FACE",FACE,{"disambiguationData":[OSD([subQ0,sQuery(id+"F2.wireOp",EDGE,"E13.7.0"),sQuery(id+"F2.wireOp",EDGE,"E13.7.1"),sQuery(id+"F2.wireOp",EDGE,"E13.7.2"),sQuery(id+"F2.wireOp",EDGE,"E13.7.3"),sQuery(id+"F2.wireOp",EDGE,"E13.7.4")])],"isStart":true}),makeQuery(id+"F3.opExtrude","CAP_FACE",FACE,{"disambiguationData":[OSD([subQ0,sQuery(id+"F2.wireOp",EDGE,"E13.8.0"),sQuery(id+"F2.wireOp",EDGE,"E13.8.1"),sQuery(id+"F2.wireOp",EDGE,"E13.8.2"),sQuery(id+"F2.wireOp",EDGE,"E13.8.3"),sQuery(id+"F2.wireOp",EDGE,"E13.8.4")])],"isStart":true}),makeQuery(id+"F3.opExtrude","CAP_FACE",FACE,{"disambiguationData":[OSD([subQ0,sQuery(id+"F2.wireOp",EDGE,"E13.9.0"),sQuery(id+"F2.wireOp",EDGE,"E13.9.1"),sQuery(id+"F2.wireOp",EDGE,"E13.9.2"),sQuery(id+"F2.wireOp",EDGE,"E13.9.3"),sQuery(id+"F2.wireOp",EDGE,"E13.9.4")])],"isStart":true}),makeQuery(id+"F3.opExtrude","CAP_FACE",FACE,{"disambiguationData":[OSD([subQ0,sQuery(id+"F2.wireOp",EDGE,"E13.10.0"),sQuery(id+"F2.wireOp",EDGE,"E13.10.1"),sQuery(id+"F2.wireOp",EDGE,"E13.10.2"),sQuery(id+"F2.wireOp",EDGE,"E13.10.3"),sQuery(id+"F2.wireOp",EDGE,"E13.10.4")])],"isStart":true}),makeQuery(id+"F3.opExtrude","CAP_FACE",FACE,{"disambiguationData":[OSD([subQ0,sQuery(id+"F2.wireOp",EDGE,"E13.11.0"),sQuery(id+"F2.wireOp",EDGE,"E13.11.1"),sQuery(id+"F2.wireOp",EDGE,"E13.11.2"),sQuery(id+"F2.wireOp",EDGE,"E13.11.3"),sQuery(id+"F2.wireOp",EDGE,"E13.11.4")])],"isStart":true}),makeQuery(id+"F3.opExtrude","CAP_FACE",FACE,{"disambiguationData":[OSD([subQ0,sQuery(id+"F2.wireOp",EDGE,"E13.12.0"),sQuery(id+"F2.wireOp",EDGE,"E13.12.1"),sQuery(id+"F2.wireOp",EDGE,"E13.12.2"),sQuery(id+"F2.wireOp",EDGE,"E13.12.3"),sQuery(id+"F2.wireOp",EDGE,"E13.12.4")])],"isStart":true}),makeQuery(id+"F3.opExtrude","CAP_FACE",FACE,{"disambiguationData":[OSD([subQ0,sQuery(id+"F2.wireOp",EDGE,"E13.13.0"),sQuery(id+"F2.wireOp",EDGE,"E13.13.1"),sQuery(id+"F2.wireOp",EDGE,"E13.13.2"),sQuery(id+"F2.wireOp",EDGE,"E13.13.3"),sQuery(id+"F2.wireOp",EDGE,"E13.13.4")])],"isStart":true}),makeQuery(id+"F3.opExtrude","CAP_FACE",FACE,{"disambiguationData":[OSD([subQ0,sQuery(id+"F2.wireOp",EDGE,"E13.14.0"),sQuery(id+"F2.wireOp",EDGE,"E13.14.1"),sQuery(id+"F2.wireOp",EDGE,"E13.14.2"),sQuery(id+"F2.wireOp",EDGE,"E13.14.3"),sQuery(id+"F2.wireOp",EDGE,"E13.14.4")])],"isStart":true}),makeQuery(id+"F3.opExtrude","CAP_FACE",FACE,{"disambiguationData":[OSD([subQ0,sQuery(id+"F2.wireOp",EDGE,"E13.15.0"),sQuery(id+"F2.wireOp",EDGE,"E13.15.1"),sQuery(id+"F2.wireOp",EDGE,"E13.15.2"),sQuery(id+"F2.wireOp",EDGE,"E13.15.3"),sQuery(id+"F2.wireOp",EDGE,"E13.15.4")])],"isStart":true}),makeQuery(id+"F3.opExtrude","CAP_FACE",FACE,{"disambiguationData":[OSD([subQ0,sQuery(id+"F2.wireOp",EDGE,"E13.16.0"),sQuery(id+"F2.wireOp",EDGE,"E13.16.1"),sQuery(id+"F2.wireOp",EDGE,"E13.16.2"),sQuery(id+"F2.wireOp",EDGE,"E13.16.3"),sQuery(id+"F2.wireOp",EDGE,"E13.16.4")])],"isStart":true}),makeQuery(id+"F3.opExtrude","CAP_FACE",FACE,{"disambiguationData":[OSD([subQ0,sQuery(id+"F2.wireOp",EDGE,"E13.17.0"),sQuery(id+"F2.wireOp",EDGE,"E13.17.1"),sQuery(id+"F2.wireOp",EDGE,"E13.17.2"),sQuery(id+"F2.wireOp",EDGE,"E13.17.3"),sQuery(id+"F2.wireOp",EDGE,"E13.17.4")])],"isStart":true}),makeQuery(id+"F3.opExtrude","CAP_FACE",FACE,{"disambiguationData":[OSD([subQ0,sQuery(id+"F2.wireOp",EDGE,"E13.18.0"),sQuery(id+"F2.wireOp",EDGE,"E13.18.1"),sQuery(id+"F2.wireOp",EDGE,"E13.18.2"),sQuery(id+"F2.wireOp",EDGE,"E13.18.3"),sQuery(id+"F2.wireOp",EDGE,"E13.18.4")])],"isStart":true}),makeQuery(id+"F3.opExtrude","CAP_FACE",FACE,{"disambiguationData":[OSD([subQ0,sQuery(id+"F2.wireOp",EDGE,"E13.19.0"),sQuery(id+"F2.wireOp",EDGE,"E13.19.1"),sQuery(id+"F2.wireOp",EDGE,"E13.19.2"),sQuery(id+"F2.wireOp",EDGE,"E13.19.3"),sQuery(id+"F2.wireOp",EDGE,"E13.19.4")])],"isStart":true}),makeQuery(id+"F3.opExtrude","CAP_FACE",FACE,{"disambiguationData":[OSD([subQ0,sQuery(id+"F2.wireOp",EDGE,"E13.20.0"),sQuery(id+"F2.wireOp",EDGE,"E13.20.1"),sQuery(id+"F2.wireOp",EDGE,"E13.20.2"),sQuery(id+"F2.wireOp",EDGE,"E13.20.3"),sQuery(id+"F2.wireOp",EDGE,"E13.20.4")])],"isStart":true}),makeQuery(id+"F3.opExtrude","CAP_FACE",FACE,{"disambiguationData":[OSD([subQ0,sQuery(id+"F2.wireOp",EDGE,"E13.21.0"),sQuery(id+"F2.wireOp",EDGE,"E13.21.1"),sQuery(id+"F2.wireOp",EDGE,"E13.21.2"),sQuery(id+"F2.wireOp",EDGE,"E13.21.3"),sQuery(id+"F2.wireOp",EDGE,"E13.21.4")])],"isStart":true}),makeQuery(id+"F3.opExtrude","CAP_FACE",FACE,{"disambiguationData":[OSD([subQ0,sQuery(id+"F2.wireOp",EDGE,"E13.22.0"),sQuery(id+"F2.wireOp",EDGE,"E13.22.1"),sQuery(id+"F2.wireOp",EDGE,"E13.22.2"),sQuery(id+"F2.wireOp",EDGE,"E13.22.3"),sQuery(id+"F2.wireOp",EDGE,"E13.22.4")])],"isStart":true}),makeQuery(id+"F3.opExtrude","CAP_FACE",FACE,{"disambiguationData":[OSD([subQ0,sQuery(id+"F2.wireOp",EDGE,"E13.23.0"),sQuery(id+"F2.wireOp",EDGE,"E13.23.1"),sQuery(id+"F2.wireOp",EDGE,"E13.23.2"),sQuery(id+"F2.wireOp",EDGE,"E13.23.3"),sQuery(id+"F2.wireOp",EDGE,"E13.23.4")])],"isStart":true}),makeQuery(id+"F3.opExtrude","CAP_FACE",FACE,{"disambiguationData":[OSD([subQ0,sQuery(id+"F2.wireOp",EDGE,"E13.24.0"),sQuery(id+"F2.wireOp",EDGE,"E13.24.1"),sQuery(id+"F2.wireOp",EDGE,"E13.24.2"),sQuery(id+"F2.wireOp",EDGE,"E13.24.3"),sQuery(id+"F2.wireOp",EDGE,"E13.24.4")])],"isStart":true}),makeQuery(id+"F3.opExtrude","CAP_FACE",FACE,{"disambiguationData":[OSD([subQ0,sQuery(id+"F2.wireOp",EDGE,"E13.25.0"),sQuery(id+"F2.wireOp",EDGE,"E13.25.1"),sQuery(id+"F2.wireOp",EDGE,"E13.25.2"),sQuery(id+"F2.wireOp",EDGE,"E13.25.3"),sQuery(id+"F2.wireOp",EDGE,"E13.25.4")])],"isStart":true}),makeQuery(id+"F3.opExtrude","CAP_FACE",FACE,{"disambiguationData":[OSD([subQ0,sQuery(id+"F2.wireOp",EDGE,"E13.26.0"),sQuery(id+"F2.wireOp",EDGE,"E13.26.1"),sQuery(id+"F2.wireOp",EDGE,"E13.26.2"),sQuery(id+"F2.wireOp",EDGE,"E13.26.3"),sQuery(id+"F2.wireOp",EDGE,"E13.26.4")])],"isStart":true}),makeQuery(id+"F3.opExtrude","CAP_FACE",FACE,{"disambiguationData":[OSD([subQ0,sQuery(id+"F2.wireOp",EDGE,"E13.27.0"),sQuery(id+"F2.wireOp",EDGE,"E13.27.1"),sQuery(id+"F2.wireOp",EDGE,"E13.27.2"),sQuery(id+"F2.wireOp",EDGE,"E13.27.3"),sQuery(id+"F2.wireOp",EDGE,"E13.27.4")])],"isStart":true}),makeQuery(id+"F3.opExtrude","CAP_FACE",FACE,{"disambiguationData":[OSD([subQ0,sQuery(id+"F2.wireOp",EDGE,"E13.28.0"),sQuery(id+"F2.wireOp",EDGE,"E13.28.1"),sQuery(id+"F2.wireOp",EDGE,"E13.28.2"),sQuery(id+"F2.wireOp",EDGE,"E13.28.3"),sQuery(id+"F2.wireOp",EDGE,"E13.28.4")])],"isStart":true}),makeQuery(id+"F3.opExtrude","CAP_FACE",FACE,{"disambiguationData":[OSD([subQ0,sQuery(id+"F2.wireOp",EDGE,"E13.29.0"),sQuery(id+"F2.wireOp",EDGE,"E13.29.1"),sQuery(id+"F2.wireOp",EDGE,"E13.29.2"),sQuery(id+"F2.wireOp",EDGE,"E13.29.3"),sQuery(id+"F2.wireOp",EDGE,"E13.29.4")])],"isStart":true}),makeQuery(id+"F3.opExtrude","CAP_FACE",FACE,{"disambiguationData":[OSD([subQ0,sQuery(id+"F2.wireOp",EDGE,"E13.30.0"),sQuery(id+"F2.wireOp",EDGE,"E13.30.1"),sQuery(id+"F2.wireOp",EDGE,"E13.30.2"),sQuery(id+"F2.wireOp",EDGE,"E13.30.3"),sQuery(id+"F2.wireOp",EDGE,"E13.30.4")])],"isStart":true}),makeQuery(id+"F3.opExtrude","CAP_FACE",FACE,{"disambiguationData":[OSD([subQ0,sQuery(id+"F2.wireOp",EDGE,"E13.31.0"),sQuery(id+"F2.wireOp",EDGE,"E13.31.1"),sQuery(id+"F2.wireOp",EDGE,"E13.31.2"),sQuery(id+"F2.wireOp",EDGE,"E13.31.3"),sQuery(id+"F2.wireOp",EDGE,"E13.31.4")])],"isStart":true})]});}
            var sketch = newSketch(context, id + "F10", { "sketchPlane" : qUnion([Q0])});
            skCircle(sketch, "E34", {"center": v(0, 0) * mm, "radius": 9 * mm});
            skSolve(sketch);
        }
        {
            var Q0;
            Q0 = qSketchRegion(id + "F10", true);
            extrude(context, id + "F11", {"entities" : qUnion([Q0]), "operationType" : NewBodyOperationType.REMOVE, "oppositeDirection" : true, "depth" : 0.5 * mm});
        }
        {
            var Q0;
            Q0=qCreatedBy(makeId("Top.planeOp"),FACE);
            var sketch = newSketch(context, id + "F12", { "sketchPlane" : qUnion([Q0])});
            skLineSegment(sketch, "E35", {"start": v(0, 0) * mm, "end": v(0, 6.81) * mm});
            skArc(sketch, "E36", {"start": v(6.5, -0.5) * mm, "mid": v(6, 0) * mm, "end": v(5.5, -0.5) * mm});
            skLineSegment(sketch, "E37", {"start": v(6.5, -0.5) * mm, "end": v(5.5, -0.5) * mm});
            skSolve(sketch);
        }
        {
            var Q0;
            Q0 = qSketchRegion(id + "F12", true);
            var Q1;
            Q1=sQuery(id+"F12.wireOp",EDGE,"E35");
            revolve(context, id + "F13", {"operationType" : NewBodyOperationType.ADD, "entities" : qUnion([Q0]), "axis" : qUnion([Q1]), "revolveType" : RevolveType.FULL});
        }
        {
            var Q0;
            Q0=makeQuery(id+"F9.opExtrude","CAP_FACE",FACE,{"disambiguationData":[OSD([sQuery(id+"F8.wireOp",EDGE,"E33")])],"isStart":false});
            var sketch = newSketch(context, id + "F14", { "sketchPlane" : qUnion([Q0])});
            skCircle(sketch, "E38", {"center": v(0, 0) * mm, "radius": 1.5 * mm});
            skSolve(sketch);
        }
        {
            var Q0;
            Q0 = qSketchRegion(id + "F14", true);
            extrude(context, id + "F15", {"entities" : qUnion([Q0]), "operationType" : NewBodyOperationType.REMOVE, "oppositeDirection" : true, "depth" : 25 * mm});
        }
    });
